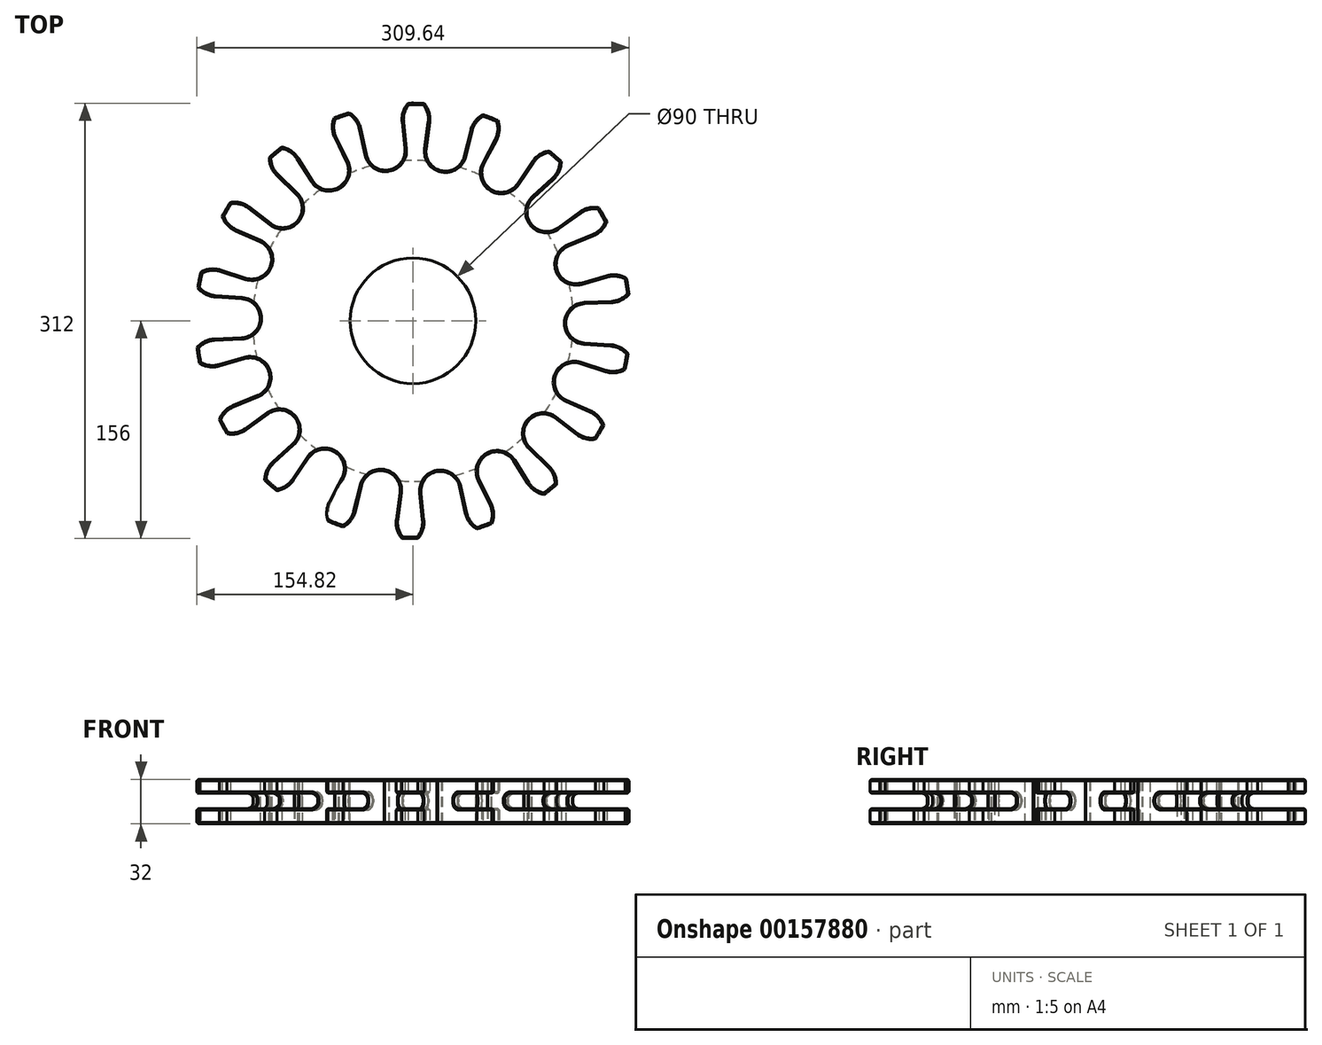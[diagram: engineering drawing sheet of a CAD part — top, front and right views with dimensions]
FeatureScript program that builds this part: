
annotation { "Feature Type Name" : "Feature", "Feature Type Description" : "" }
export const myFeature = defineFeature(function(context is Context, id is Id, definition is map)
    precondition{}
    {
        {
            var Q0;
            Q0=qCreatedBy(makeId("Top.planeOp"),FACE);
            var sketch = newSketch(context, id + "F0", { "sketchPlane" : qUnion([Q0])});
            skCircle(sketch, "E0", {"center": v(0, 0) * mm, "radius": 158.3 * mm, "construction": true});
            skArc(sketch, "E1", {"start": v(-102.28, 39.14) * mm, "mid": v(-102.55, 49.4) * mm, "end": v(-109.74, 56.72) * mm});
            skLineSegment(sketch, "E2", {"start": v(-109.74, 56.72) * mm, "end": v(-127.33, 64.55) * mm});
            skArc(sketch, "E3", {"start": v(-127.33, 64.55) * mm, "mid": v(-133.16, 68.77) * mm, "end": v(-136.8, 74.97) * mm});
            skArc(sketch, "E4", {"start": v(-136.8, 74.97) * mm, "mid": v(-133.95, 79.96) * mm, "end": v(-130.91, 84.84) * mm});
            skArc(sketch, "E5", {"start": v(-130.91, 84.84) * mm, "mid": v(-123.72, 84.58) * mm, "end": v(-117.25, 81.44) * mm});
            skLineSegment(sketch, "E6", {"start": v(-117.25, 81.44) * mm, "end": v(-102, 69.68) * mm});
            skArc(sketch, "E7", {"start": v(-102, 69.68) * mm, "mid": v(-92.15, 66.82) * mm, "end": v(-83, 71.46) * mm});
            skLineSegment(sketch, "E8", {"start": v(-83, 71.46) * mm, "end": v(-82.72, 71.76) * mm});
            skArc(sketch, "E9", {"start": v(-82.72, 71.76) * mm, "mid": v(-79.47, 81.5) * mm, "end": v(-83.72, 90.83) * mm});
            skLineSegment(sketch, "E10", {"start": v(-83.72, 90.83) * mm, "end": v(-97.57, 104.2) * mm});
            skArc(sketch, "E11", {"start": v(-97.57, 104.2) * mm, "mid": v(-101.6, 110.16) * mm, "end": v(-102.91, 117.24) * mm});
            skArc(sketch, "E12", {"start": v(-102.91, 117.24) * mm, "mid": v(-98.52, 120.95) * mm, "end": v(-94, 124.5) * mm});
            skArc(sketch, "E13", {"start": v(-94, 124.5) * mm, "mid": v(-87.33, 121.8) * mm, "end": v(-82.32, 116.63) * mm});
            skLineSegment(sketch, "E14", {"start": v(-82.32, 116.63) * mm, "end": v(-72.02, 100.36) * mm});
            skArc(sketch, "E15", {"start": v(-72.02, 100.36) * mm, "mid": v(-63.74, 94.31) * mm, "end": v(-53.55, 95.53) * mm});
            skLineSegment(sketch, "E16", {"start": v(-53.55, 95.53) * mm, "end": v(-53.2, 95.73) * mm});
            skArc(sketch, "E17", {"start": v(-53.2, 95.73) * mm, "mid": v(-46.8, 103.76) * mm, "end": v(-47.6, 113.99) * mm});
            skLineSegment(sketch, "E18", {"start": v(-47.6, 113.99) * mm, "end": v(-56.04, 131.3) * mm});
            skArc(sketch, "E19", {"start": v(-56.04, 131.3) * mm, "mid": v(-57.8, 138.27) * mm, "end": v(-56.6, 145.37) * mm});
            skArc(sketch, "E20", {"start": v(-56.6, 145.37) * mm, "mid": v(-51.21, 147.35) * mm, "end": v(-45.75, 149.14) * mm});
            skArc(sketch, "E21", {"start": v(-45.75, 149.14) * mm, "mid": v(-40.41, 144.32) * mm, "end": v(-37.46, 137.75) * mm});
            skLineSegment(sketch, "E22", {"start": v(-37.46, 137.75) * mm, "end": v(-33.35, 118.94) * mm});
            skArc(sketch, "E23", {"start": v(-33.35, 118.94) * mm, "mid": v(-27.64, 110.42) * mm, "end": v(-17.64, 108.08) * mm});
            skLineSegment(sketch, "E24", {"start": v(-17.64, 108.08) * mm, "end": v(-17.24, 108.15) * mm});
            skArc(sketch, "E25", {"start": v(-17.24, 108.15) * mm, "mid": v(-8.5, 113.5) * mm, "end": v(-5.75, 123.4) * mm});
            skLineSegment(sketch, "E26", {"start": v(-5.75, 123.4) * mm, "end": v(-7.76, 142.55) * mm});
            skArc(sketch, "E27", {"start": v(-7.76, 142.55) * mm, "mid": v(-7.02, 149.7) * mm, "end": v(-3.48, 155.96) * mm});
            skArc(sketch, "E28", {"start": v(-3.48, 155.96) * mm, "mid": v(2.27, 155.98) * mm, "end": v(8.02, 155.8) * mm});
            skArc(sketch, "E29", {"start": v(8.02, 155.8) * mm, "mid": v(11.38, 149.43) * mm, "end": v(11.9, 142.26) * mm});
            skLineSegment(sketch, "E30", {"start": v(11.9, 142.26) * mm, "end": v(9.34, 123.18) * mm});
            skArc(sketch, "E31", {"start": v(9.34, 123.18) * mm, "mid": v(11.8, 113.21) * mm, "end": v(20.39, 107.6) * mm});
            skLineSegment(sketch, "E32", {"start": v(20.39, 107.6) * mm, "end": v(20.79, 107.52) * mm});
            skArc(sketch, "E33", {"start": v(20.79, 107.52) * mm, "mid": v(30.84, 109.57) * mm, "end": v(36.8, 117.92) * mm});
            skLineSegment(sketch, "E34", {"start": v(36.8, 117.92) * mm, "end": v(41.46, 136.6) * mm});
            skArc(sketch, "E35", {"start": v(41.46, 136.6) * mm, "mid": v(44.6, 143.08) * mm, "end": v(50.07, 147.74) * mm});
            skArc(sketch, "E36", {"start": v(50.07, 147.74) * mm, "mid": v(55.49, 145.8) * mm, "end": v(60.82, 143.65) * mm});
            skArc(sketch, "E37", {"start": v(60.82, 143.65) * mm, "mid": v(61.8, 136.53) * mm, "end": v(59.85, 129.6) * mm});
            skLineSegment(sketch, "E38", {"start": v(59.85, 129.6) * mm, "end": v(50.9, 112.55) * mm});
            skArc(sketch, "E39", {"start": v(50.9, 112.55) * mm, "mid": v(49.8, 102.35) * mm, "end": v(55.96, 94.14) * mm});
            skLineSegment(sketch, "E40", {"start": v(55.96, 94.14) * mm, "end": v(56.3, 93.93) * mm});
            skArc(sketch, "E41", {"start": v(56.3, 93.93) * mm, "mid": v(66.46, 92.41) * mm, "end": v(74.91, 98.22) * mm});
            skLineSegment(sketch, "E42", {"start": v(74.91, 98.22) * mm, "end": v(85.68, 114.18) * mm});
            skArc(sketch, "E43", {"start": v(85.68, 114.18) * mm, "mid": v(90.85, 119.2) * mm, "end": v(97.59, 121.7) * mm});
            skArc(sketch, "E44", {"start": v(97.59, 121.7) * mm, "mid": v(102, 118.03) * mm, "end": v(106.29, 114.19) * mm});
            skArc(sketch, "E45", {"start": v(106.29, 114.19) * mm, "mid": v(104.77, 107.16) * mm, "end": v(100.56, 101.32) * mm});
            skLineSegment(sketch, "E46", {"start": v(100.56, 101.32) * mm, "end": v(86.33, 88.35) * mm});
            skArc(sketch, "E47", {"start": v(86.33, 88.35) * mm, "mid": v(81.8, 79.14) * mm, "end": v(84.78, 69.32) * mm});
            skLineSegment(sketch, "E48", {"start": v(84.78, 69.32) * mm, "end": v(85.04, 69) * mm});
            skArc(sketch, "E49", {"start": v(85.04, 69) * mm, "mid": v(94.06, 64.1) * mm, "end": v(104, 66.68) * mm});
            skLineSegment(sketch, "E50", {"start": v(104, 66.68) * mm, "end": v(119.57, 78) * mm});
            skArc(sketch, "E51", {"start": v(119.57, 78) * mm, "mid": v(126.13, 80.93) * mm, "end": v(133.33, 81) * mm});
            skArc(sketch, "E52", {"start": v(133.33, 81) * mm, "mid": v(136.22, 76.02) * mm, "end": v(138.93, 70.95) * mm});
            skArc(sketch, "E53", {"start": v(138.93, 70.95) * mm, "mid": v(135.1, 64.86) * mm, "end": v(129.15, 60.82) * mm});
            skLineSegment(sketch, "E54", {"start": v(129.15, 60.82) * mm, "end": v(111.35, 53.5) * mm});
            skArc(sketch, "E55", {"start": v(111.35, 53.5) * mm, "mid": v(103.94, 46.4) * mm, "end": v(103.38, 36.15) * mm});
            skLineSegment(sketch, "E56", {"start": v(103.38, 36.15) * mm, "end": v(103.51, 35.76) * mm});
            skArc(sketch, "E57", {"start": v(103.51, 35.76) * mm, "mid": v(110.31, 28.07) * mm, "end": v(120.52, 27.09) * mm});
            skLineSegment(sketch, "E58", {"start": v(120.52, 27.09) * mm, "end": v(139.03, 32.4) * mm});
            skArc(sketch, "E59", {"start": v(139.03, 32.4) * mm, "mid": v(146.2, 32.91) * mm, "end": v(152.99, 30.5) * mm});
            skArc(sketch, "E60", {"start": v(152.99, 30.5) * mm, "mid": v(154, 24.85) * mm, "end": v(154.82, 19.15) * mm});
            skArc(sketch, "E61", {"start": v(154.82, 19.15) * mm, "mid": v(149.14, 14.74) * mm, "end": v(142.17, 12.98) * mm});
            skLineSegment(sketch, "E62", {"start": v(142.17, 12.98) * mm, "end": v(122.93, 12.19) * mm});
            skArc(sketch, "E63", {"start": v(122.93, 12.19) * mm, "mid": v(113.54, 8.04) * mm, "end": v(109.5, -1.4) * mm});
            skLineSegment(sketch, "E64", {"start": v(109.5, -1.4) * mm, "end": v(109.5, -1.8) * mm});
            skArc(sketch, "E65", {"start": v(109.5, -1.8) * mm, "mid": v(113.26, -11.35) * mm, "end": v(122.52, -15.77) * mm});
            skLineSegment(sketch, "E66", {"start": v(122.52, -15.77) * mm, "end": v(141.73, -17.11) * mm});
            skArc(sketch, "E67", {"start": v(141.73, -17.11) * mm, "mid": v(148.65, -19.08) * mm, "end": v(154.2, -23.66) * mm});
            skArc(sketch, "E68", {"start": v(154.2, -23.66) * mm, "mid": v(153.22, -29.33) * mm, "end": v(152.03, -34.95) * mm});
            skArc(sketch, "E69", {"start": v(152.03, -34.95) * mm, "mid": v(145.19, -37.16) * mm, "end": v(138.03, -36.43) * mm});
            skLineSegment(sketch, "E70", {"start": v(138.03, -36.43) * mm, "end": v(119.68, -30.6) * mm});
            skArc(sketch, "E71", {"start": v(119.68, -30.6) * mm, "mid": v(109.45, -31.28) * mm, "end": v(102.43, -38.76) * mm});
            skLineSegment(sketch, "E72", {"start": v(102.43, -38.76) * mm, "end": v(102.28, -39.14) * mm});
            skArc(sketch, "E73", {"start": v(102.28, -39.14) * mm, "mid": v(102.55, -49.4) * mm, "end": v(109.74, -56.72) * mm});
            skLineSegment(sketch, "E74", {"start": v(109.74, -56.72) * mm, "end": v(127.33, -64.55) * mm});
            skArc(sketch, "E75", {"start": v(127.33, -64.55) * mm, "mid": v(133.16, -68.77) * mm, "end": v(136.8, -74.97) * mm});
            skArc(sketch, "E76", {"start": v(136.8, -74.97) * mm, "mid": v(133.95, -79.96) * mm, "end": v(130.91, -84.84) * mm});
            skArc(sketch, "E77", {"start": v(130.91, -84.84) * mm, "mid": v(123.72, -84.58) * mm, "end": v(117.25, -81.44) * mm});
            skLineSegment(sketch, "E78", {"start": v(117.25, -81.44) * mm, "end": v(102, -69.68) * mm});
            skArc(sketch, "E79", {"start": v(102, -69.68) * mm, "mid": v(92.15, -66.82) * mm, "end": v(83, -71.46) * mm});
            skLineSegment(sketch, "E80", {"start": v(83, -71.46) * mm, "end": v(82.72, -71.76) * mm});
            skArc(sketch, "E81", {"start": v(82.72, -71.76) * mm, "mid": v(79.47, -81.5) * mm, "end": v(83.72, -90.83) * mm});
            skLineSegment(sketch, "E82", {"start": v(83.72, -90.83) * mm, "end": v(97.57, -104.2) * mm});
            skArc(sketch, "E83", {"start": v(97.57, -104.2) * mm, "mid": v(101.6, -110.16) * mm, "end": v(102.91, -117.24) * mm});
            skArc(sketch, "E84", {"start": v(102.91, -117.24) * mm, "mid": v(98.52, -120.95) * mm, "end": v(94, -124.5) * mm});
            skArc(sketch, "E85", {"start": v(94, -124.5) * mm, "mid": v(87.33, -121.8) * mm, "end": v(82.32, -116.63) * mm});
            skLineSegment(sketch, "E86", {"start": v(82.32, -116.63) * mm, "end": v(72.02, -100.36) * mm});
            skArc(sketch, "E87", {"start": v(72.02, -100.36) * mm, "mid": v(63.74, -94.31) * mm, "end": v(53.55, -95.53) * mm});
            skLineSegment(sketch, "E88", {"start": v(53.55, -95.53) * mm, "end": v(53.2, -95.73) * mm});
            skArc(sketch, "E89", {"start": v(53.2, -95.73) * mm, "mid": v(46.8, -103.76) * mm, "end": v(47.6, -113.99) * mm});
            skLineSegment(sketch, "E90", {"start": v(47.6, -113.99) * mm, "end": v(56.04, -131.3) * mm});
            skArc(sketch, "E91", {"start": v(56.04, -131.3) * mm, "mid": v(57.8, -138.27) * mm, "end": v(56.6, -145.37) * mm});
            skArc(sketch, "E92", {"start": v(56.6, -145.37) * mm, "mid": v(51.21, -147.35) * mm, "end": v(45.75, -149.14) * mm});
            skArc(sketch, "E93", {"start": v(45.75, -149.14) * mm, "mid": v(40.41, -144.32) * mm, "end": v(37.46, -137.75) * mm});
            skLineSegment(sketch, "E94", {"start": v(37.46, -137.75) * mm, "end": v(33.35, -118.94) * mm});
            skArc(sketch, "E95", {"start": v(33.35, -118.94) * mm, "mid": v(27.64, -110.42) * mm, "end": v(17.64, -108.08) * mm});
            skLineSegment(sketch, "E96", {"start": v(17.64, -108.08) * mm, "end": v(17.24, -108.15) * mm});
            skArc(sketch, "E97", {"start": v(17.24, -108.15) * mm, "mid": v(8.5, -113.5) * mm, "end": v(5.75, -123.4) * mm});
            skLineSegment(sketch, "E98", {"start": v(5.75, -123.4) * mm, "end": v(7.76, -142.55) * mm});
            skArc(sketch, "E99", {"start": v(7.76, -142.55) * mm, "mid": v(7.02, -149.7) * mm, "end": v(3.48, -155.96) * mm});
            skArc(sketch, "E100", {"start": v(3.48, -155.96) * mm, "mid": v(-2.27, -155.98) * mm, "end": v(-8.02, -155.8) * mm});
            skArc(sketch, "E101", {"start": v(-8.02, -155.8) * mm, "mid": v(-11.38, -149.43) * mm, "end": v(-11.9, -142.26) * mm});
            skLineSegment(sketch, "E102", {"start": v(-11.9, -142.26) * mm, "end": v(-9.34, -123.18) * mm});
            skArc(sketch, "E103", {"start": v(-9.34, -123.18) * mm, "mid": v(-11.8, -113.21) * mm, "end": v(-20.39, -107.6) * mm});
            skLineSegment(sketch, "E104", {"start": v(-20.39, -107.6) * mm, "end": v(-20.79, -107.52) * mm});
            skArc(sketch, "E105", {"start": v(-20.79, -107.52) * mm, "mid": v(-30.84, -109.57) * mm, "end": v(-36.8, -117.92) * mm});
            skLineSegment(sketch, "E106", {"start": v(-36.8, -117.92) * mm, "end": v(-41.46, -136.6) * mm});
            skArc(sketch, "E107", {"start": v(-41.46, -136.6) * mm, "mid": v(-44.6, -143.08) * mm, "end": v(-50.07, -147.74) * mm});
            skArc(sketch, "E108", {"start": v(-50.07, -147.74) * mm, "mid": v(-55.49, -145.8) * mm, "end": v(-60.82, -143.65) * mm});
            skArc(sketch, "E109", {"start": v(-60.82, -143.65) * mm, "mid": v(-61.8, -136.53) * mm, "end": v(-59.85, -129.6) * mm});
            skLineSegment(sketch, "E110", {"start": v(-59.85, -129.6) * mm, "end": v(-50.9, -112.55) * mm});
            skArc(sketch, "E111", {"start": v(-50.9, -112.55) * mm, "mid": v(-49.8, -102.35) * mm, "end": v(-55.96, -94.14) * mm});
            skLineSegment(sketch, "E112", {"start": v(-55.96, -94.14) * mm, "end": v(-56.3, -93.93) * mm});
            skArc(sketch, "E113", {"start": v(-56.3, -93.93) * mm, "mid": v(-66.46, -92.41) * mm, "end": v(-74.91, -98.22) * mm});
            skLineSegment(sketch, "E114", {"start": v(-74.91, -98.22) * mm, "end": v(-85.68, -114.18) * mm});
            skArc(sketch, "E115", {"start": v(-85.68, -114.18) * mm, "mid": v(-90.85, -119.2) * mm, "end": v(-97.59, -121.7) * mm});
            skArc(sketch, "E116", {"start": v(-97.59, -121.7) * mm, "mid": v(-102, -118.03) * mm, "end": v(-106.29, -114.19) * mm});
            skArc(sketch, "E117", {"start": v(-106.29, -114.19) * mm, "mid": v(-104.77, -107.16) * mm, "end": v(-100.56, -101.32) * mm});
            skLineSegment(sketch, "E118", {"start": v(-100.56, -101.32) * mm, "end": v(-86.33, -88.35) * mm});
            skArc(sketch, "E119", {"start": v(-86.33, -88.35) * mm, "mid": v(-81.8, -79.14) * mm, "end": v(-84.78, -69.32) * mm});
            skLineSegment(sketch, "E120", {"start": v(-84.78, -69.32) * mm, "end": v(-85.04, -69) * mm});
            skArc(sketch, "E121", {"start": v(-85.04, -69) * mm, "mid": v(-94.06, -64.1) * mm, "end": v(-104, -66.68) * mm});
            skLineSegment(sketch, "E122", {"start": v(-104, -66.68) * mm, "end": v(-119.57, -78) * mm});
            skArc(sketch, "E123", {"start": v(-119.57, -78) * mm, "mid": v(-126.13, -80.93) * mm, "end": v(-133.33, -81) * mm});
            skArc(sketch, "E124", {"start": v(-133.33, -81) * mm, "mid": v(-136.22, -76.02) * mm, "end": v(-138.93, -70.95) * mm});
            skArc(sketch, "E125", {"start": v(-138.93, -70.95) * mm, "mid": v(-135.1, -64.86) * mm, "end": v(-129.15, -60.82) * mm});
            skLineSegment(sketch, "E126", {"start": v(-129.15, -60.82) * mm, "end": v(-111.35, -53.5) * mm});
            skArc(sketch, "E127", {"start": v(-111.35, -53.5) * mm, "mid": v(-103.94, -46.4) * mm, "end": v(-103.38, -36.15) * mm});
            skLineSegment(sketch, "E128", {"start": v(-103.38, -36.15) * mm, "end": v(-103.51, -35.76) * mm});
            skArc(sketch, "E129", {"start": v(-103.51, -35.76) * mm, "mid": v(-110.31, -28.07) * mm, "end": v(-120.52, -27.09) * mm});
            skLineSegment(sketch, "E130", {"start": v(-120.52, -27.09) * mm, "end": v(-139.03, -32.4) * mm});
            skArc(sketch, "E131", {"start": v(-139.03, -32.4) * mm, "mid": v(-146.2, -32.91) * mm, "end": v(-152.99, -30.5) * mm});
            skArc(sketch, "E132", {"start": v(-152.99, -30.5) * mm, "mid": v(-154, -24.85) * mm, "end": v(-154.82, -19.15) * mm});
            skArc(sketch, "E133", {"start": v(-154.82, -19.15) * mm, "mid": v(-149.14, -14.74) * mm, "end": v(-142.17, -12.98) * mm});
            skLineSegment(sketch, "E134", {"start": v(-142.17, -12.98) * mm, "end": v(-122.93, -12.19) * mm});
            skArc(sketch, "E135", {"start": v(-122.93, -12.19) * mm, "mid": v(-113.54, -8.04) * mm, "end": v(-109.5, 1.4) * mm});
            skLineSegment(sketch, "E136", {"start": v(-109.5, 1.4) * mm, "end": v(-109.5, 1.8) * mm});
            skArc(sketch, "E137", {"start": v(-109.5, 1.8) * mm, "mid": v(-113.26, 11.35) * mm, "end": v(-122.52, 15.77) * mm});
            skLineSegment(sketch, "E138", {"start": v(-122.52, 15.77) * mm, "end": v(-141.73, 17.11) * mm});
            skArc(sketch, "E139", {"start": v(-141.73, 17.11) * mm, "mid": v(-148.65, 19.08) * mm, "end": v(-154.2, 23.66) * mm});
            skArc(sketch, "E140", {"start": v(-154.2, 23.66) * mm, "mid": v(-153.22, 29.33) * mm, "end": v(-152.03, 34.95) * mm});
            skArc(sketch, "E141", {"start": v(-152.03, 34.95) * mm, "mid": v(-145.19, 37.16) * mm, "end": v(-138.03, 36.43) * mm});
            skLineSegment(sketch, "E142", {"start": v(-138.03, 36.43) * mm, "end": v(-119.68, 30.6) * mm});
            skArc(sketch, "E143", {"start": v(-119.68, 30.6) * mm, "mid": v(-109.45, 31.28) * mm, "end": v(-102.43, 38.76) * mm});
            skLineSegment(sketch, "E144", {"start": v(-102.43, 38.76) * mm, "end": v(-102.28, 39.14) * mm});
            skCircle(sketch, "E145", {"center": v(0, 0) * mm, "radius": 74.9 * mm, "construction": true});
            skSolve(sketch);
        }
        {
            var Q0;
            Q0=qSketchRegion(id+"F0",true);
            extrude(context, id + "F1", {"entities" : qUnion([Q0]), "endBound" : BoundingType.SYMMETRIC, "depth" : 32 * mm});
        }
        {
            var Q0;
            Q0=qCreatedBy(makeId("Top.planeOp"),FACE);
            var sketch = newSketch(context, id + "F2", { "sketchPlane" : qUnion([Q0])});
            skCircle(sketch, "E146", {"center": v(0, 0) * mm, "radius": 45 * mm});
            skSolve(sketch);
        }
        {
            var Q0;
            Q0=qSketchRegion(id+"F2",true);
            extrude(context, id + "F3", {"entities" : qUnion([Q0]), "operationType" : NewBodyOperationType.REMOVE, "endBound" : BoundingType.SYMMETRIC, "oppositeDirection" : true, "depth" : 91.5 * mm});
        }
        {
            var Q0;
            Q0=qCreatedBy(makeId("Right.planeOp"),FACE);
            var sketch = newSketch(context, id + "F4", { "sketchPlane" : qUnion([Q0])});
            skLineSegment(sketch, "E147.bottom", {"start": v(-163.5, 6) * mm, "end": v(-119.5, 6) * mm});
            skLineSegment(sketch, "E147.top", {"start": v(-163.5, -5) * mm, "end": v(-119.5, -5) * mm});
            skLineSegment(sketch, "E147.left", {"start": v(-163.5, 6) * mm, "end": v(-163.5, -5) * mm});
            skLineSegment(sketch, "E147.right", {"start": v(-115, 1.5) * mm, "end": v(-115, -0.5) * mm});
            skPoint(sketch, "E148.visualSharp", {"position": v(-115, 6) * mm});
            skArc(sketch, "E148.filletArc", {"start": v(-115, 1.5) * mm, "mid": v(-116.32, 4.68) * mm, "end": v(-119.5, 6) * mm});
            skPoint(sketch, "E149.visualSharp", {"position": v(-115, -5) * mm});
            skArc(sketch, "E149.filletArc", {"start": v(-119.5, -5) * mm, "mid": v(-116.32, -3.68) * mm, "end": v(-115, -0.5) * mm});
            skSolve(sketch);
        }
        {
            var Q0;
            Q0=qSketchRegion(id+"F4",true);
            var Q1;
            Q1=makeQuery(id+"F3.boolean.opBoolean","COPY",FACE,{"derivedFrom":makeQuery(id+"F3.opExtrude","SWEPT_FACE",FACE,{"disambiguationData":[OSD([sQuery(id+"F2.wireOp",EDGE,"E146")])]})});
            revolve(context, id + "F5", {"operationType" : NewBodyOperationType.REMOVE, "entities" : qUnion([Q0]), "axis" : qUnion([Q1]), "revolveType" : RevolveType.FULL, "oppositeDirection" : true});
        }
        {
            var Q0;
            Q0=makeQuery(id+"F1.opExtrude","CAP_EDGE",EDGE,{"disambiguationData":[OSD([sQuery(id+"F0.wireOp",EDGE,"E113")])],"isStart":false});
            var Q1;
            Q1=makeQuery(id+"F1.opExtrude","CAP_EDGE",EDGE,{"disambiguationData":[OSD([sQuery(id+"F0.wireOp",EDGE,"E121")])],"isStart":false});
            var Q2;
            Q2=makeQuery(id+"F1.opExtrude","CAP_EDGE",EDGE,{"disambiguationData":[OSD([sQuery(id+"F0.wireOp",EDGE,"E129")])],"isStart":false});
            var Q3;
            Q3=makeQuery(id+"F1.opExtrude","CAP_EDGE",EDGE,{"disambiguationData":[OSD([sQuery(id+"F0.wireOp",EDGE,"E137")])],"isStart":false});
            var Q4;
            Q4=makeQuery(id+"F1.opExtrude","CAP_EDGE",EDGE,{"disambiguationData":[OSD([sQuery(id+"F0.wireOp",EDGE,"E1")])],"isStart":false});
            var Q5;
            Q5=makeQuery(id+"F1.opExtrude","CAP_EDGE",EDGE,{"disambiguationData":[OSD([sQuery(id+"F0.wireOp",EDGE,"E9")])],"isStart":false});
            var Q6;
            Q6=makeQuery(id+"F1.opExtrude","CAP_EDGE",EDGE,{"disambiguationData":[OSD([sQuery(id+"F0.wireOp",EDGE,"E17")])],"isStart":false});
            var Q7;
            Q7=makeQuery(id+"F1.opExtrude","CAP_EDGE",EDGE,{"disambiguationData":[OSD([sQuery(id+"F0.wireOp",EDGE,"E25")])],"isStart":false});
            var Q8;
            Q8=makeQuery(id+"F1.opExtrude","CAP_EDGE",EDGE,{"disambiguationData":[OSD([sQuery(id+"F0.wireOp",EDGE,"E33")])],"isStart":false});
            var Q9;
            Q9=makeQuery(id+"F1.opExtrude","CAP_EDGE",EDGE,{"disambiguationData":[OSD([sQuery(id+"F0.wireOp",EDGE,"E41")])],"isStart":false});
            var Q10;
            Q10=makeQuery(id+"F1.opExtrude","CAP_EDGE",EDGE,{"disambiguationData":[OSD([sQuery(id+"F0.wireOp",EDGE,"E50")])],"isStart":false});
            var Q11;
            Q11=makeQuery(id+"F1.opExtrude","CAP_EDGE",EDGE,{"disambiguationData":[OSD([sQuery(id+"F0.wireOp",EDGE,"E58")])],"isStart":false});
            var Q12;
            Q12=makeQuery(id+"F1.opExtrude","CAP_EDGE",EDGE,{"disambiguationData":[OSD([sQuery(id+"F0.wireOp",EDGE,"E65")])],"isStart":false});
            var Q13;
            Q13=makeQuery(id+"F1.opExtrude","CAP_EDGE",EDGE,{"disambiguationData":[OSD([sQuery(id+"F0.wireOp",EDGE,"E73")])],"isStart":false});
            var Q14;
            Q14=makeQuery(id+"F1.opExtrude","CAP_EDGE",EDGE,{"disambiguationData":[OSD([sQuery(id+"F0.wireOp",EDGE,"E81")])],"isStart":false});
            var Q15;
            Q15=makeQuery(id+"F1.opExtrude","CAP_EDGE",EDGE,{"disambiguationData":[OSD([sQuery(id+"F0.wireOp",EDGE,"E89")])],"isStart":false});
            var Q16;
            Q16=makeQuery(id+"F1.opExtrude","CAP_EDGE",EDGE,{"disambiguationData":[OSD([sQuery(id+"F0.wireOp",EDGE,"E97")])],"isStart":false});
            var Q17;
            Q17=makeQuery(id+"F1.opExtrude","CAP_EDGE",EDGE,{"disambiguationData":[OSD([sQuery(id+"F0.wireOp",EDGE,"E105")])],"isStart":false});
            var Q18;
            Q18=makeQuery(id+"F1.opExtrude","CAP_EDGE",EDGE,{"disambiguationData":[OSD([sQuery(id+"F0.wireOp",EDGE,"E103")])],"isStart":false});
            var Q19;
            Q19=makeQuery(id+"F1.opExtrude","CAP_EDGE",EDGE,{"disambiguationData":[OSD([sQuery(id+"F0.wireOp",EDGE,"E95")])],"isStart":false});
            var Q20;
            Q20=makeQuery(id+"F1.opExtrude","CAP_EDGE",EDGE,{"disambiguationData":[OSD([sQuery(id+"F0.wireOp",EDGE,"E87")])],"isStart":false});
            var Q21;
            Q21=makeQuery(id+"F1.opExtrude","CAP_EDGE",EDGE,{"disambiguationData":[OSD([sQuery(id+"F0.wireOp",EDGE,"E79")])],"isStart":false});
            var Q22;
            Q22=makeQuery(id+"F1.opExtrude","CAP_EDGE",EDGE,{"disambiguationData":[OSD([sQuery(id+"F0.wireOp",EDGE,"E71")])],"isStart":false});
            var Q23;
            Q23=makeQuery(id+"F1.opExtrude","CAP_EDGE",EDGE,{"disambiguationData":[OSD([sQuery(id+"F0.wireOp",EDGE,"E63")])],"isStart":false});
            var Q24;
            Q24=makeQuery(id+"F1.opExtrude","CAP_EDGE",EDGE,{"disambiguationData":[OSD([sQuery(id+"F0.wireOp",EDGE,"E55")])],"isStart":false});
            var Q25;
            Q25=makeQuery(id+"F1.opExtrude","CAP_EDGE",EDGE,{"disambiguationData":[OSD([sQuery(id+"F0.wireOp",EDGE,"E47")])],"isStart":false});
            var Q26;
            Q26=makeQuery(id+"F1.opExtrude","CAP_EDGE",EDGE,{"disambiguationData":[OSD([sQuery(id+"F0.wireOp",EDGE,"E119")])],"isStart":false});
            var Q27;
            Q27=makeQuery(id+"F1.opExtrude","CAP_EDGE",EDGE,{"disambiguationData":[OSD([sQuery(id+"F0.wireOp",EDGE,"E127")])],"isStart":false});
            var Q28;
            Q28=makeQuery(id+"F1.opExtrude","CAP_EDGE",EDGE,{"disambiguationData":[OSD([sQuery(id+"F0.wireOp",EDGE,"E135")])],"isStart":false});
            var Q29;
            Q29=makeQuery(id+"F1.opExtrude","CAP_EDGE",EDGE,{"disambiguationData":[OSD([sQuery(id+"F0.wireOp",EDGE,"E143")])],"isStart":false});
            var Q30;
            Q30=makeQuery(id+"F1.opExtrude","CAP_EDGE",EDGE,{"disambiguationData":[OSD([sQuery(id+"F0.wireOp",EDGE,"E7")])],"isStart":false});
            var Q31;
            Q31=makeQuery(id+"F1.opExtrude","CAP_EDGE",EDGE,{"disambiguationData":[OSD([sQuery(id+"F0.wireOp",EDGE,"E15")])],"isStart":false});
            var Q32;
            Q32=makeQuery(id+"F1.opExtrude","CAP_EDGE",EDGE,{"disambiguationData":[OSD([sQuery(id+"F0.wireOp",EDGE,"E23")])],"isStart":false});
            var Q33;
            Q33=makeQuery(id+"F1.opExtrude","CAP_EDGE",EDGE,{"disambiguationData":[OSD([sQuery(id+"F0.wireOp",EDGE,"E31")])],"isStart":false});
            var Q34;
            Q34=makeQuery(id+"F1.opExtrude","CAP_EDGE",EDGE,{"disambiguationData":[OSD([sQuery(id+"F0.wireOp",EDGE,"E39")])],"isStart":false});
            var Q35;
            Q35=makeQuery(id+"F1.opExtrude","CAP_EDGE",EDGE,{"disambiguationData":[OSD([sQuery(id+"F0.wireOp",EDGE,"E100")])],"isStart":false});
            var Q36;
            Q36=makeQuery(id+"F1.opExtrude","CAP_EDGE",EDGE,{"disambiguationData":[OSD([sQuery(id+"F0.wireOp",EDGE,"E108")])],"isStart":false});
            var Q37;
            Q37=makeQuery(id+"F1.opExtrude","CAP_EDGE",EDGE,{"disambiguationData":[OSD([sQuery(id+"F0.wireOp",EDGE,"E116")])],"isStart":false});
            var Q38;
            Q38=makeQuery(id+"F1.opExtrude","CAP_EDGE",EDGE,{"disambiguationData":[OSD([sQuery(id+"F0.wireOp",EDGE,"E124")])],"isStart":false});
            var Q39;
            Q39=makeQuery(id+"F1.opExtrude","CAP_EDGE",EDGE,{"disambiguationData":[OSD([sQuery(id+"F0.wireOp",EDGE,"E132")])],"isStart":false});
            var Q40;
            Q40=makeQuery(id+"F1.opExtrude","CAP_EDGE",EDGE,{"disambiguationData":[OSD([sQuery(id+"F0.wireOp",EDGE,"E140")])],"isStart":false});
            var Q41;
            Q41=makeQuery(id+"F1.opExtrude","CAP_EDGE",EDGE,{"disambiguationData":[OSD([sQuery(id+"F0.wireOp",EDGE,"E4")])],"isStart":false});
            var Q42;
            Q42=makeQuery(id+"F1.opExtrude","CAP_EDGE",EDGE,{"disambiguationData":[OSD([sQuery(id+"F0.wireOp",EDGE,"E12")])],"isStart":false});
            var Q43;
            Q43=makeQuery(id+"F1.opExtrude","CAP_EDGE",EDGE,{"disambiguationData":[OSD([sQuery(id+"F0.wireOp",EDGE,"E20")])],"isStart":false});
            var Q44;
            Q44=makeQuery(id+"F1.opExtrude","CAP_EDGE",EDGE,{"disambiguationData":[OSD([sQuery(id+"F0.wireOp",EDGE,"E28")])],"isStart":false});
            var Q45;
            Q45=makeQuery(id+"F1.opExtrude","CAP_EDGE",EDGE,{"disambiguationData":[OSD([sQuery(id+"F0.wireOp",EDGE,"E36")])],"isStart":false});
            var Q46;
            Q46=makeQuery(id+"F1.opExtrude","CAP_EDGE",EDGE,{"disambiguationData":[OSD([sQuery(id+"F0.wireOp",EDGE,"E44")])],"isStart":false});
            var Q47;
            Q47=makeQuery(id+"F1.opExtrude","CAP_EDGE",EDGE,{"disambiguationData":[OSD([sQuery(id+"F0.wireOp",EDGE,"E52")])],"isStart":false});
            var Q48;
            Q48=makeQuery(id+"F1.opExtrude","CAP_EDGE",EDGE,{"disambiguationData":[OSD([sQuery(id+"F0.wireOp",EDGE,"E60")])],"isStart":false});
            var Q49;
            Q49=makeQuery(id+"F1.opExtrude","CAP_EDGE",EDGE,{"disambiguationData":[OSD([sQuery(id+"F0.wireOp",EDGE,"E68")])],"isStart":false});
            var Q50;
            Q50=makeQuery(id+"F1.opExtrude","CAP_EDGE",EDGE,{"disambiguationData":[OSD([sQuery(id+"F0.wireOp",EDGE,"E76")])],"isStart":false});
            var Q51;
            Q51=makeQuery(id+"F1.opExtrude","CAP_EDGE",EDGE,{"disambiguationData":[OSD([sQuery(id+"F0.wireOp",EDGE,"E84")])],"isStart":false});
            var Q52;
            Q52=makeQuery(id+"F1.opExtrude","CAP_EDGE",EDGE,{"disambiguationData":[OSD([sQuery(id+"F0.wireOp",EDGE,"E92")])],"isStart":false});
            var Q53;
            Q53=makeQuery(id+"F5.boolean.opBoolean","INTERSECT",EDGE,{"derivedFrom":[makeQuery(id+"F1.opExtrude","SWEPT_FACE",FACE,{"disambiguationData":[OSD([sQuery(id+"F0.wireOp",EDGE,"E89")])]}),makeQuery(id+"F5.opRevolve","SWEPT_FACE",FACE,{"disambiguationData":[OSD([sQuery(id+"F4.wireOp",EDGE,"E149.filletArc")])]})]});
            var Q54;
            Q54=makeQuery(id+"F5.boolean.opBoolean","INTERSECT",EDGE,{"derivedFrom":[makeQuery(id+"F1.opExtrude","SWEPT_FACE",FACE,{"disambiguationData":[OSD([sQuery(id+"F0.wireOp",EDGE,"E81")])]}),makeQuery(id+"F5.opRevolve","SWEPT_FACE",FACE,{"disambiguationData":[OSD([sQuery(id+"F4.wireOp",EDGE,"E149.filletArc")])]})]});
            var Q55;
            Q55=makeQuery(id+"F5.boolean.opBoolean","INTERSECT",EDGE,{"derivedFrom":[makeQuery(id+"F1.opExtrude","SWEPT_FACE",FACE,{"disambiguationData":[OSD([sQuery(id+"F0.wireOp",EDGE,"E79")])]}),makeQuery(id+"F5.opRevolve","SWEPT_FACE",FACE,{"disambiguationData":[OSD([sQuery(id+"F4.wireOp",EDGE,"E149.filletArc")])]})]});
            var Q56;
            Q56=makeQuery(id+"F5.boolean.opBoolean","INTERSECT",EDGE,{"derivedFrom":[makeQuery(id+"F1.opExtrude","SWEPT_FACE",FACE,{"disambiguationData":[OSD([sQuery(id+"F0.wireOp",EDGE,"E87")])]}),makeQuery(id+"F5.opRevolve","SWEPT_FACE",FACE,{"disambiguationData":[OSD([sQuery(id+"F4.wireOp",EDGE,"E149.filletArc")])]})]});
            var Q57;
            Q57=makeQuery(id+"F5.boolean.opBoolean","INTERSECT",EDGE,{"derivedFrom":[makeQuery(id+"F1.opExtrude","SWEPT_FACE",FACE,{"disambiguationData":[OSD([sQuery(id+"F0.wireOp",EDGE,"E95")])]}),makeQuery(id+"F5.opRevolve","SWEPT_FACE",FACE,{"disambiguationData":[OSD([sQuery(id+"F4.wireOp",EDGE,"E149.filletArc")])]})]});
            var Q58;
            Q58=makeQuery(id+"F5.boolean.opBoolean","INTERSECT",EDGE,{"derivedFrom":[makeQuery(id+"F1.opExtrude","SWEPT_FACE",FACE,{"disambiguationData":[OSD([sQuery(id+"F0.wireOp",EDGE,"E97")])]}),makeQuery(id+"F5.opRevolve","SWEPT_FACE",FACE,{"disambiguationData":[OSD([sQuery(id+"F4.wireOp",EDGE,"E149.filletArc")])]})]});
            var Q59;
            Q59=makeQuery(id+"F5.boolean.opBoolean","INTERSECT",EDGE,{"derivedFrom":[makeQuery(id+"F1.opExtrude","SWEPT_FACE",FACE,{"disambiguationData":[OSD([sQuery(id+"F0.wireOp",EDGE,"E105")])]}),makeQuery(id+"F5.opRevolve","SWEPT_FACE",FACE,{"disambiguationData":[OSD([sQuery(id+"F4.wireOp",EDGE,"E149.filletArc")])]})]});
            var Q60;
            Q60=makeQuery(id+"F5.boolean.opBoolean","INTERSECT",EDGE,{"derivedFrom":[makeQuery(id+"F1.opExtrude","SWEPT_FACE",FACE,{"disambiguationData":[OSD([sQuery(id+"F0.wireOp",EDGE,"E103")])]}),makeQuery(id+"F5.opRevolve","SWEPT_FACE",FACE,{"disambiguationData":[OSD([sQuery(id+"F4.wireOp",EDGE,"E149.filletArc")])]})]});
            var Q61;
            Q61=makeQuery(id+"F5.boolean.opBoolean","INTERSECT",EDGE,{"derivedFrom":[makeQuery(id+"F1.opExtrude","SWEPT_FACE",FACE,{"disambiguationData":[OSD([sQuery(id+"F0.wireOp",EDGE,"E111")])]}),makeQuery(id+"F5.opRevolve","SWEPT_FACE",FACE,{"disambiguationData":[OSD([sQuery(id+"F4.wireOp",EDGE,"E149.filletArc")])]})]});
            var Q62;
            Q62=makeQuery(id+"F5.boolean.opBoolean","INTERSECT",EDGE,{"derivedFrom":[makeQuery(id+"F1.opExtrude","SWEPT_FACE",FACE,{"disambiguationData":[OSD([sQuery(id+"F0.wireOp",EDGE,"E119")])]}),makeQuery(id+"F5.opRevolve","SWEPT_FACE",FACE,{"disambiguationData":[OSD([sQuery(id+"F4.wireOp",EDGE,"E149.filletArc")])]})]});
            var Q63;
            Q63=makeQuery(id+"F5.boolean.opBoolean","INTERSECT",EDGE,{"derivedFrom":[makeQuery(id+"F1.opExtrude","SWEPT_FACE",FACE,{"disambiguationData":[OSD([sQuery(id+"F0.wireOp",EDGE,"E121")])]}),makeQuery(id+"F5.opRevolve","SWEPT_FACE",FACE,{"disambiguationData":[OSD([sQuery(id+"F4.wireOp",EDGE,"E149.filletArc")])]})]});
            var Q64;
            Q64=makeQuery(id+"F5.boolean.opBoolean","INTERSECT",EDGE,{"derivedFrom":[makeQuery(id+"F1.opExtrude","SWEPT_FACE",FACE,{"disambiguationData":[OSD([sQuery(id+"F0.wireOp",EDGE,"E113")])]}),makeQuery(id+"F5.opRevolve","SWEPT_FACE",FACE,{"disambiguationData":[OSD([sQuery(id+"F4.wireOp",EDGE,"E149.filletArc")])]})]});
            var Q65;
            Q65=makeQuery(id+"F5.boolean.opBoolean","INTERSECT",EDGE,{"derivedFrom":[makeQuery(id+"F1.opExtrude","SWEPT_FACE",FACE,{"disambiguationData":[OSD([sQuery(id+"F0.wireOp",EDGE,"E129")])]}),makeQuery(id+"F5.opRevolve","SWEPT_FACE",FACE,{"disambiguationData":[OSD([sQuery(id+"F4.wireOp",EDGE,"E149.filletArc")])]})]});
            var Q66;
            Q66=makeQuery(id+"F5.boolean.opBoolean","INTERSECT",EDGE,{"derivedFrom":[makeQuery(id+"F1.opExtrude","SWEPT_FACE",FACE,{"disambiguationData":[OSD([sQuery(id+"F0.wireOp",EDGE,"E137")])]}),makeQuery(id+"F5.opRevolve","SWEPT_FACE",FACE,{"disambiguationData":[OSD([sQuery(id+"F4.wireOp",EDGE,"E149.filletArc")])]})]});
            var Q67;
            Q67=makeQuery(id+"F5.boolean.opBoolean","INTERSECT",EDGE,{"derivedFrom":[makeQuery(id+"F1.opExtrude","SWEPT_FACE",FACE,{"disambiguationData":[OSD([sQuery(id+"F0.wireOp",EDGE,"E127")])]}),makeQuery(id+"F5.opRevolve","SWEPT_FACE",FACE,{"disambiguationData":[OSD([sQuery(id+"F4.wireOp",EDGE,"E149.filletArc")])]})]});
            var Q68;
            Q68=makeQuery(id+"F5.boolean.opBoolean","INTERSECT",EDGE,{"derivedFrom":[makeQuery(id+"F1.opExtrude","SWEPT_FACE",FACE,{"disambiguationData":[OSD([sQuery(id+"F0.wireOp",EDGE,"E135")])]}),makeQuery(id+"F5.opRevolve","SWEPT_FACE",FACE,{"disambiguationData":[OSD([sQuery(id+"F4.wireOp",EDGE,"E149.filletArc")])]})]});
            var Q69;
            Q69=makeQuery(id+"F5.boolean.opBoolean","INTERSECT",EDGE,{"derivedFrom":[makeQuery(id+"F1.opExtrude","SWEPT_FACE",FACE,{"disambiguationData":[OSD([sQuery(id+"F0.wireOp",EDGE,"E7")])]}),makeQuery(id+"F5.opRevolve","SWEPT_FACE",FACE,{"disambiguationData":[OSD([sQuery(id+"F4.wireOp",EDGE,"E149.filletArc")])]})]});
            var Q70;
            Q70=makeQuery(id+"F5.boolean.opBoolean","INTERSECT",EDGE,{"derivedFrom":[makeQuery(id+"F1.opExtrude","SWEPT_FACE",FACE,{"disambiguationData":[OSD([sQuery(id+"F0.wireOp",EDGE,"E143")])]}),makeQuery(id+"F5.opRevolve","SWEPT_FACE",FACE,{"disambiguationData":[OSD([sQuery(id+"F4.wireOp",EDGE,"E149.filletArc")])]})]});
            var Q71;
            Q71=makeQuery(id+"F5.boolean.opBoolean","INTERSECT",EDGE,{"derivedFrom":[makeQuery(id+"F1.opExtrude","SWEPT_FACE",FACE,{"disambiguationData":[OSD([sQuery(id+"F0.wireOp",EDGE,"E17")])]}),makeQuery(id+"F5.opRevolve","SWEPT_FACE",FACE,{"disambiguationData":[OSD([sQuery(id+"F4.wireOp",EDGE,"E149.filletArc")])]})]});
            var Q72;
            Q72=makeQuery(id+"F5.boolean.opBoolean","INTERSECT",EDGE,{"derivedFrom":[makeQuery(id+"F1.opExtrude","SWEPT_FACE",FACE,{"disambiguationData":[OSD([sQuery(id+"F0.wireOp",EDGE,"E9")])]}),makeQuery(id+"F5.opRevolve","SWEPT_FACE",FACE,{"disambiguationData":[OSD([sQuery(id+"F4.wireOp",EDGE,"E149.filletArc")])]})]});
            var Q73;
            Q73=makeQuery(id+"F5.boolean.opBoolean","INTERSECT",EDGE,{"derivedFrom":[makeQuery(id+"F1.opExtrude","SWEPT_FACE",FACE,{"disambiguationData":[OSD([sQuery(id+"F0.wireOp",EDGE,"E1")])]}),makeQuery(id+"F5.opRevolve","SWEPT_FACE",FACE,{"disambiguationData":[OSD([sQuery(id+"F4.wireOp",EDGE,"E149.filletArc")])]})]});
            var Q74;
            Q74=makeQuery(id+"F5.boolean.opBoolean","INTERSECT",EDGE,{"derivedFrom":[makeQuery(id+"F1.opExtrude","SWEPT_FACE",FACE,{"disambiguationData":[OSD([sQuery(id+"F0.wireOp",EDGE,"E124")])]}),makeQuery(id+"F5.opRevolve","SWEPT_FACE",FACE,{"disambiguationData":[OSD([sQuery(id+"F4.wireOp",EDGE,"E147.top")])]})]});
            var Q75;
            Q75=makeQuery(id+"F5.boolean.opBoolean","INTERSECT",EDGE,{"derivedFrom":[makeQuery(id+"F1.opExtrude","SWEPT_FACE",FACE,{"disambiguationData":[OSD([sQuery(id+"F0.wireOp",EDGE,"E132")])]}),makeQuery(id+"F5.opRevolve","SWEPT_FACE",FACE,{"disambiguationData":[OSD([sQuery(id+"F4.wireOp",EDGE,"E147.top")])]})]});
            var Q76;
            Q76=makeQuery(id+"F5.boolean.opBoolean","INTERSECT",EDGE,{"derivedFrom":[makeQuery(id+"F1.opExtrude","SWEPT_FACE",FACE,{"disambiguationData":[OSD([sQuery(id+"F0.wireOp",EDGE,"E124")])]}),makeQuery(id+"F5.opRevolve","SWEPT_FACE",FACE,{"disambiguationData":[OSD([sQuery(id+"F4.wireOp",EDGE,"E147.bottom")])]})]});
            var Q77;
            Q77=makeQuery(id+"F5.boolean.opBoolean","INTERSECT",EDGE,{"derivedFrom":[makeQuery(id+"F1.opExtrude","SWEPT_FACE",FACE,{"disambiguationData":[OSD([sQuery(id+"F0.wireOp",EDGE,"E116")])]}),makeQuery(id+"F5.opRevolve","SWEPT_FACE",FACE,{"disambiguationData":[OSD([sQuery(id+"F4.wireOp",EDGE,"E147.top")])]})]});
            var Q78;
            Q78=makeQuery(id+"F5.boolean.opBoolean","INTERSECT",EDGE,{"derivedFrom":[makeQuery(id+"F1.opExtrude","SWEPT_FACE",FACE,{"disambiguationData":[OSD([sQuery(id+"F0.wireOp",EDGE,"E116")])]}),makeQuery(id+"F5.opRevolve","SWEPT_FACE",FACE,{"disambiguationData":[OSD([sQuery(id+"F4.wireOp",EDGE,"E147.bottom")])]})]});
            var Q79;
            Q79=makeQuery(id+"F5.boolean.opBoolean","INTERSECT",EDGE,{"derivedFrom":[makeQuery(id+"F1.opExtrude","SWEPT_FACE",FACE,{"disambiguationData":[OSD([sQuery(id+"F0.wireOp",EDGE,"E108")])]}),makeQuery(id+"F5.opRevolve","SWEPT_FACE",FACE,{"disambiguationData":[OSD([sQuery(id+"F4.wireOp",EDGE,"E147.top")])]})]});
            var Q80;
            Q80=makeQuery(id+"F5.boolean.opBoolean","INTERSECT",EDGE,{"derivedFrom":[makeQuery(id+"F1.opExtrude","SWEPT_FACE",FACE,{"disambiguationData":[OSD([sQuery(id+"F0.wireOp",EDGE,"E108")])]}),makeQuery(id+"F5.opRevolve","SWEPT_FACE",FACE,{"disambiguationData":[OSD([sQuery(id+"F4.wireOp",EDGE,"E147.bottom")])]})]});
            var Q81;
            Q81=makeQuery(id+"F1.opExtrude","CAP_EDGE",EDGE,{"disambiguationData":[OSD([sQuery(id+"F0.wireOp",EDGE,"E72")])],"isStart":false});
            var Q82;
            Q82=makeQuery(id+"F1.opExtrude","CAP_EDGE",EDGE,{"disambiguationData":[OSD([sQuery(id+"F0.wireOp",EDGE,"E64")])],"isStart":false});
            var Q83;
            Q83=makeQuery(id+"F1.opExtrude","CAP_EDGE",EDGE,{"disambiguationData":[OSD([sQuery(id+"F0.wireOp",EDGE,"E56")])],"isStart":false});
            var Q84;
            Q84=makeQuery(id+"F5.boolean.opBoolean","INTERSECT",EDGE,{"derivedFrom":[makeQuery(id+"F1.opExtrude","SWEPT_FACE",FACE,{"disambiguationData":[OSD([sQuery(id+"F0.wireOp",EDGE,"E55")])]}),makeQuery(id+"F5.opRevolve","SWEPT_FACE",FACE,{"disambiguationData":[OSD([sQuery(id+"F4.wireOp",EDGE,"E149.filletArc")])]})]});
            var Q85;
            Q85=makeQuery(id+"F5.boolean.opBoolean","INTERSECT",EDGE,{"derivedFrom":[makeQuery(id+"F1.opExtrude","SWEPT_FACE",FACE,{"disambiguationData":[OSD([sQuery(id+"F0.wireOp",EDGE,"E47")])]}),makeQuery(id+"F5.opRevolve","SWEPT_FACE",FACE,{"disambiguationData":[OSD([sQuery(id+"F4.wireOp",EDGE,"E149.filletArc")])]})]});
            var Q86;
            Q86=makeQuery(id+"F5.boolean.opBoolean","INTERSECT",EDGE,{"derivedFrom":[makeQuery(id+"F1.opExtrude","SWEPT_FACE",FACE,{"disambiguationData":[OSD([sQuery(id+"F0.wireOp",EDGE,"E63")])]}),makeQuery(id+"F5.opRevolve","SWEPT_FACE",FACE,{"disambiguationData":[OSD([sQuery(id+"F4.wireOp",EDGE,"E149.filletArc")])]})]});
            var Q87;
            Q87=makeQuery(id+"F5.boolean.opBoolean","INTERSECT",EDGE,{"derivedFrom":[makeQuery(id+"F1.opExtrude","SWEPT_FACE",FACE,{"disambiguationData":[OSD([sQuery(id+"F0.wireOp",EDGE,"E71")])]}),makeQuery(id+"F5.opRevolve","SWEPT_FACE",FACE,{"disambiguationData":[OSD([sQuery(id+"F4.wireOp",EDGE,"E149.filletArc")])]})]});
            var Q88;
            Q88=makeQuery(id+"F1.opExtrude","CAP_EDGE",EDGE,{"disambiguationData":[OSD([sQuery(id+"F0.wireOp",EDGE,"E16")])],"isStart":false});
            var Q89;
            Q89=makeQuery(id+"F1.opExtrude","CAP_EDGE",EDGE,{"disambiguationData":[OSD([sQuery(id+"F0.wireOp",EDGE,"E24")])],"isStart":false});
            var Q90;
            Q90=makeQuery(id+"F1.opExtrude","CAP_EDGE",EDGE,{"disambiguationData":[OSD([sQuery(id+"F0.wireOp",EDGE,"E32")])],"isStart":false});
            var Q91;
            Q91=makeQuery(id+"F1.opExtrude","CAP_EDGE",EDGE,{"disambiguationData":[OSD([sQuery(id+"F0.wireOp",EDGE,"E40")])],"isStart":false});
            var Q92;
            Q92=makeQuery(id+"F1.opExtrude","CAP_EDGE",EDGE,{"disambiguationData":[OSD([sQuery(id+"F0.wireOp",EDGE,"E48")])],"isStart":false});
            var Q93;
            Q93=makeQuery(id+"F1.opExtrude","CAP_EDGE",EDGE,{"disambiguationData":[OSD([sQuery(id+"F0.wireOp",EDGE,"E80")])],"isStart":false});
            var Q94;
            Q94=makeQuery(id+"F1.opExtrude","CAP_EDGE",EDGE,{"disambiguationData":[OSD([sQuery(id+"F0.wireOp",EDGE,"E88")])],"isStart":false});
            var Q95;
            Q95=makeQuery(id+"F1.opExtrude","CAP_EDGE",EDGE,{"disambiguationData":[OSD([sQuery(id+"F0.wireOp",EDGE,"E96")])],"isStart":false});
            var Q96;
            Q96=makeQuery(id+"F1.opExtrude","CAP_EDGE",EDGE,{"disambiguationData":[OSD([sQuery(id+"F0.wireOp",EDGE,"E104")])],"isStart":false});
            var Q97;
            Q97=makeQuery(id+"F1.opExtrude","CAP_EDGE",EDGE,{"disambiguationData":[OSD([sQuery(id+"F0.wireOp",EDGE,"E112")])],"isStart":false});
            var Q98;
            Q98=makeQuery(id+"F1.opExtrude","CAP_EDGE",EDGE,{"disambiguationData":[OSD([sQuery(id+"F0.wireOp",EDGE,"E120")])],"isStart":false});
            var Q99;
            Q99=makeQuery(id+"F1.opExtrude","CAP_EDGE",EDGE,{"disambiguationData":[OSD([sQuery(id+"F0.wireOp",EDGE,"E128")])],"isStart":false});
            var Q100;
            Q100=makeQuery(id+"F1.opExtrude","CAP_EDGE",EDGE,{"disambiguationData":[OSD([sQuery(id+"F0.wireOp",EDGE,"E136")])],"isStart":false});
            var Q101;
            Q101=makeQuery(id+"F1.opExtrude","CAP_EDGE",EDGE,{"disambiguationData":[OSD([sQuery(id+"F0.wireOp",EDGE,"E144")])],"isStart":false});
            var Q102;
            Q102=makeQuery(id+"F1.opExtrude","CAP_EDGE",EDGE,{"disambiguationData":[OSD([sQuery(id+"F0.wireOp",EDGE,"E8")])],"isStart":false});
            var Q103;
            Q103=makeQuery(id+"F1.opExtrude","CAP_EDGE",EDGE,{"disambiguationData":[OSD([sQuery(id+"F0.wireOp",EDGE,"E82")])],"isStart":true});
            var Q104;
            Q104=makeQuery(id+"F1.opExtrude","CAP_EDGE",EDGE,{"disambiguationData":[OSD([sQuery(id+"F0.wireOp",EDGE,"E90")])],"isStart":true});
            var Q105;
            Q105=makeQuery(id+"F1.opExtrude","CAP_EDGE",EDGE,{"disambiguationData":[OSD([sQuery(id+"F0.wireOp",EDGE,"E98")])],"isStart":true});
            var Q106;
            Q106=makeQuery(id+"F1.opExtrude","CAP_EDGE",EDGE,{"disambiguationData":[OSD([sQuery(id+"F0.wireOp",EDGE,"E106")])],"isStart":true});
            var Q107;
            Q107=makeQuery(id+"F1.opExtrude","CAP_EDGE",EDGE,{"disambiguationData":[OSD([sQuery(id+"F0.wireOp",EDGE,"E114")])],"isStart":true});
            var Q108;
            Q108=makeQuery(id+"F1.opExtrude","CAP_EDGE",EDGE,{"disambiguationData":[OSD([sQuery(id+"F0.wireOp",EDGE,"E122")])],"isStart":true});
            var Q109;
            Q109=makeQuery(id+"F1.opExtrude","CAP_EDGE",EDGE,{"disambiguationData":[OSD([sQuery(id+"F0.wireOp",EDGE,"E130")])],"isStart":true});
            var Q110;
            Q110=makeQuery(id+"F1.opExtrude","CAP_EDGE",EDGE,{"disambiguationData":[OSD([sQuery(id+"F0.wireOp",EDGE,"E138")])],"isStart":true});
            var Q111;
            Q111=makeQuery(id+"F1.opExtrude","CAP_EDGE",EDGE,{"disambiguationData":[OSD([sQuery(id+"F0.wireOp",EDGE,"E2")])],"isStart":true});
            var Q112;
            Q112=makeQuery(id+"F1.opExtrude","CAP_EDGE",EDGE,{"disambiguationData":[OSD([sQuery(id+"F0.wireOp",EDGE,"E10")])],"isStart":true});
            var Q113;
            Q113=makeQuery(id+"F1.opExtrude","CAP_EDGE",EDGE,{"disambiguationData":[OSD([sQuery(id+"F0.wireOp",EDGE,"E18")])],"isStart":true});
            var Q114;
            Q114=makeQuery(id+"F1.opExtrude","CAP_EDGE",EDGE,{"disambiguationData":[OSD([sQuery(id+"F0.wireOp",EDGE,"E26")])],"isStart":true});
            var Q115;
            Q115=makeQuery(id+"F1.opExtrude","CAP_EDGE",EDGE,{"disambiguationData":[OSD([sQuery(id+"F0.wireOp",EDGE,"E34")])],"isStart":true});
            var Q116;
            Q116=makeQuery(id+"F1.opExtrude","CAP_EDGE",EDGE,{"disambiguationData":[OSD([sQuery(id+"F0.wireOp",EDGE,"E22")])],"isStart":true});
            var Q117;
            Q117=makeQuery(id+"F1.opExtrude","CAP_EDGE",EDGE,{"disambiguationData":[OSD([sQuery(id+"F0.wireOp",EDGE,"E30")])],"isStart":true});
            var Q118;
            Q118=makeQuery(id+"F1.opExtrude","CAP_EDGE",EDGE,{"disambiguationData":[OSD([sQuery(id+"F0.wireOp",EDGE,"E38")])],"isStart":true});
            var Q119;
            Q119=makeQuery(id+"F1.opExtrude","CAP_EDGE",EDGE,{"disambiguationData":[OSD([sQuery(id+"F0.wireOp",EDGE,"E46")])],"isStart":true});
            var Q120;
            Q120=makeQuery(id+"F1.opExtrude","CAP_EDGE",EDGE,{"disambiguationData":[OSD([sQuery(id+"F0.wireOp",EDGE,"E54")])],"isStart":true});
            var Q121;
            Q121=makeQuery(id+"F1.opExtrude","CAP_EDGE",EDGE,{"disambiguationData":[OSD([sQuery(id+"F0.wireOp",EDGE,"E62")])],"isStart":true});
            var Q122;
            Q122=makeQuery(id+"F1.opExtrude","CAP_EDGE",EDGE,{"disambiguationData":[OSD([sQuery(id+"F0.wireOp",EDGE,"E70")])],"isStart":true});
            var Q123;
            Q123=makeQuery(id+"F1.opExtrude","CAP_EDGE",EDGE,{"disambiguationData":[OSD([sQuery(id+"F0.wireOp",EDGE,"E78")])],"isStart":true});
            var Q124;
            Q124=makeQuery(id+"F1.opExtrude","CAP_EDGE",EDGE,{"disambiguationData":[OSD([sQuery(id+"F0.wireOp",EDGE,"E86")])],"isStart":true});
            var Q125;
            Q125=makeQuery(id+"F1.opExtrude","CAP_EDGE",EDGE,{"disambiguationData":[OSD([sQuery(id+"F0.wireOp",EDGE,"E94")])],"isStart":true});
            var Q126;
            Q126=makeQuery(id+"F1.opExtrude","CAP_EDGE",EDGE,{"disambiguationData":[OSD([sQuery(id+"F0.wireOp",EDGE,"E102")])],"isStart":true});
            var Q127;
            Q127=makeQuery(id+"F1.opExtrude","CAP_EDGE",EDGE,{"disambiguationData":[OSD([sQuery(id+"F0.wireOp",EDGE,"E110")])],"isStart":true});
            var Q128;
            Q128=makeQuery(id+"F1.opExtrude","CAP_EDGE",EDGE,{"disambiguationData":[OSD([sQuery(id+"F0.wireOp",EDGE,"E118")])],"isStart":true});
            var Q129;
            Q129=makeQuery(id+"F1.opExtrude","CAP_EDGE",EDGE,{"disambiguationData":[OSD([sQuery(id+"F0.wireOp",EDGE,"E126")])],"isStart":true});
            var Q130;
            Q130=makeQuery(id+"F1.opExtrude","CAP_EDGE",EDGE,{"disambiguationData":[OSD([sQuery(id+"F0.wireOp",EDGE,"E134")])],"isStart":true});
            var Q131;
            Q131=makeQuery(id+"F1.opExtrude","CAP_EDGE",EDGE,{"disambiguationData":[OSD([sQuery(id+"F0.wireOp",EDGE,"E142")])],"isStart":true});
            var Q132;
            Q132=makeQuery(id+"F1.opExtrude","CAP_EDGE",EDGE,{"disambiguationData":[OSD([sQuery(id+"F0.wireOp",EDGE,"E6")])],"isStart":true});
            var Q133;
            Q133=makeQuery(id+"F1.opExtrude","CAP_EDGE",EDGE,{"disambiguationData":[OSD([sQuery(id+"F0.wireOp",EDGE,"E74")])],"isStart":true});
            var Q134;
            Q134=makeQuery(id+"F1.opExtrude","CAP_EDGE",EDGE,{"disambiguationData":[OSD([sQuery(id+"F0.wireOp",EDGE,"E66")])],"isStart":true});
            var Q135;
            Q135=makeQuery(id+"F1.opExtrude","CAP_EDGE",EDGE,{"disambiguationData":[OSD([sQuery(id+"F0.wireOp",EDGE,"E42")])],"isStart":true});
            var Q136;
            Q136=makeQuery(id+"F1.opExtrude","CAP_EDGE",EDGE,{"disambiguationData":[OSD([sQuery(id+"F0.wireOp",EDGE,"E14")])],"isStart":true});
            var Q137;
            Q137=makeQuery(id+"F1.opExtrude","CAP_EDGE",EDGE,{"disambiguationData":[OSD([sQuery(id+"F0.wireOp",EDGE,"E28")])],"isStart":true});
            var Q138;
            Q138=makeQuery(id+"F1.opExtrude","CAP_EDGE",EDGE,{"disambiguationData":[OSD([sQuery(id+"F0.wireOp",EDGE,"E20")])],"isStart":true});
            var Q139;
            Q139=makeQuery(id+"F1.opExtrude","CAP_EDGE",EDGE,{"disambiguationData":[OSD([sQuery(id+"F0.wireOp",EDGE,"E12")])],"isStart":true});
            var Q140;
            Q140=makeQuery(id+"F1.opExtrude","CAP_EDGE",EDGE,{"disambiguationData":[OSD([sQuery(id+"F0.wireOp",EDGE,"E4")])],"isStart":true});
            var Q141;
            Q141=makeQuery(id+"F1.opExtrude","CAP_EDGE",EDGE,{"disambiguationData":[OSD([sQuery(id+"F0.wireOp",EDGE,"E36")])],"isStart":true});
            var Q142;
            Q142=makeQuery(id+"F1.opExtrude","CAP_EDGE",EDGE,{"disambiguationData":[OSD([sQuery(id+"F0.wireOp",EDGE,"E44")])],"isStart":true});
            var Q143;
            Q143=makeQuery(id+"F1.opExtrude","CAP_EDGE",EDGE,{"disambiguationData":[OSD([sQuery(id+"F0.wireOp",EDGE,"E52")])],"isStart":true});
            var Q144;
            Q144=makeQuery(id+"F1.opExtrude","CAP_EDGE",EDGE,{"disambiguationData":[OSD([sQuery(id+"F0.wireOp",EDGE,"E60")])],"isStart":true});
            var Q145;
            Q145=makeQuery(id+"F1.opExtrude","CAP_EDGE",EDGE,{"disambiguationData":[OSD([sQuery(id+"F0.wireOp",EDGE,"E68")])],"isStart":true});
            var Q146;
            Q146=makeQuery(id+"F1.opExtrude","CAP_EDGE",EDGE,{"disambiguationData":[OSD([sQuery(id+"F0.wireOp",EDGE,"E76")])],"isStart":true});
            var Q147;
            Q147=makeQuery(id+"F1.opExtrude","CAP_EDGE",EDGE,{"disambiguationData":[OSD([sQuery(id+"F0.wireOp",EDGE,"E84")])],"isStart":true});
            var Q148;
            Q148=makeQuery(id+"F1.opExtrude","CAP_EDGE",EDGE,{"disambiguationData":[OSD([sQuery(id+"F0.wireOp",EDGE,"E92")])],"isStart":true});
            var Q149;
            Q149=makeQuery(id+"F1.opExtrude","CAP_EDGE",EDGE,{"disambiguationData":[OSD([sQuery(id+"F0.wireOp",EDGE,"E100")])],"isStart":true});
            var Q150;
            Q150=makeQuery(id+"F1.opExtrude","CAP_EDGE",EDGE,{"disambiguationData":[OSD([sQuery(id+"F0.wireOp",EDGE,"E108")])],"isStart":true});
            var Q151;
            Q151=makeQuery(id+"F1.opExtrude","CAP_EDGE",EDGE,{"disambiguationData":[OSD([sQuery(id+"F0.wireOp",EDGE,"E116")])],"isStart":true});
            var Q152;
            Q152=makeQuery(id+"F1.opExtrude","CAP_EDGE",EDGE,{"disambiguationData":[OSD([sQuery(id+"F0.wireOp",EDGE,"E124")])],"isStart":true});
            var Q153;
            Q153=makeQuery(id+"F1.opExtrude","CAP_EDGE",EDGE,{"disambiguationData":[OSD([sQuery(id+"F0.wireOp",EDGE,"E132")])],"isStart":true});
            var Q154;
            Q154=makeQuery(id+"F1.opExtrude","CAP_EDGE",EDGE,{"disambiguationData":[OSD([sQuery(id+"F0.wireOp",EDGE,"E140")])],"isStart":true});
            var Q155;
            Q155=makeQuery(id+"F1.opExtrude","CAP_EDGE",EDGE,{"disambiguationData":[OSD([sQuery(id+"F0.wireOp",EDGE,"E58")])],"isStart":true});
            var Q156;
            Q156=makeQuery(id+"F1.opExtrude","CAP_EDGE",EDGE,{"disambiguationData":[OSD([sQuery(id+"F0.wireOp",EDGE,"E50")])],"isStart":true});
            var Q157;
            Q157=makeQuery(id+"F1.opExtrude","CAP_EDGE",EDGE,{"disambiguationData":[OSD([sQuery(id+"F0.wireOp",EDGE,"E56")])],"isStart":true});
            var Q158;
            Q158=makeQuery(id+"F1.opExtrude","CAP_EDGE",EDGE,{"disambiguationData":[OSD([sQuery(id+"F0.wireOp",EDGE,"E64")])],"isStart":true});
            var Q159;
            Q159=makeQuery(id+"F1.opExtrude","CAP_EDGE",EDGE,{"disambiguationData":[OSD([sQuery(id+"F0.wireOp",EDGE,"E72")])],"isStart":true});
            var Q160;
            Q160=makeQuery(id+"F1.opExtrude","CAP_EDGE",EDGE,{"disambiguationData":[OSD([sQuery(id+"F0.wireOp",EDGE,"E80")])],"isStart":true});
            var Q161;
            Q161=makeQuery(id+"F1.opExtrude","CAP_EDGE",EDGE,{"disambiguationData":[OSD([sQuery(id+"F0.wireOp",EDGE,"E88")])],"isStart":true});
            var Q162;
            Q162=makeQuery(id+"F1.opExtrude","CAP_EDGE",EDGE,{"disambiguationData":[OSD([sQuery(id+"F0.wireOp",EDGE,"E96")])],"isStart":true});
            var Q163;
            Q163=makeQuery(id+"F1.opExtrude","CAP_EDGE",EDGE,{"disambiguationData":[OSD([sQuery(id+"F0.wireOp",EDGE,"E104")])],"isStart":true});
            var Q164;
            Q164=makeQuery(id+"F1.opExtrude","CAP_EDGE",EDGE,{"disambiguationData":[OSD([sQuery(id+"F0.wireOp",EDGE,"E112")])],"isStart":true});
            var Q165;
            Q165=makeQuery(id+"F1.opExtrude","CAP_EDGE",EDGE,{"disambiguationData":[OSD([sQuery(id+"F0.wireOp",EDGE,"E120")])],"isStart":true});
            var Q166;
            Q166=makeQuery(id+"F1.opExtrude","CAP_EDGE",EDGE,{"disambiguationData":[OSD([sQuery(id+"F0.wireOp",EDGE,"E128")])],"isStart":true});
            var Q167;
            Q167=makeQuery(id+"F1.opExtrude","CAP_EDGE",EDGE,{"disambiguationData":[OSD([sQuery(id+"F0.wireOp",EDGE,"E136")])],"isStart":true});
            var Q168;
            Q168=makeQuery(id+"F1.opExtrude","CAP_EDGE",EDGE,{"disambiguationData":[OSD([sQuery(id+"F0.wireOp",EDGE,"E144")])],"isStart":true});
            var Q169;
            Q169=makeQuery(id+"F1.opExtrude","CAP_EDGE",EDGE,{"disambiguationData":[OSD([sQuery(id+"F0.wireOp",EDGE,"E40")])],"isStart":true});
            var Q170;
            Q170=makeQuery(id+"F1.opExtrude","CAP_EDGE",EDGE,{"disambiguationData":[OSD([sQuery(id+"F0.wireOp",EDGE,"E48")])],"isStart":true});
            var Q171;
            Q171=makeQuery(id+"F1.opExtrude","CAP_EDGE",EDGE,{"disambiguationData":[OSD([sQuery(id+"F0.wireOp",EDGE,"E32")])],"isStart":true});
            var Q172;
            Q172=makeQuery(id+"F1.opExtrude","CAP_EDGE",EDGE,{"disambiguationData":[OSD([sQuery(id+"F0.wireOp",EDGE,"E24")])],"isStart":true});
            var Q173;
            Q173=makeQuery(id+"F1.opExtrude","CAP_EDGE",EDGE,{"disambiguationData":[OSD([sQuery(id+"F0.wireOp",EDGE,"E16")])],"isStart":true});
            var Q174;
            Q174=makeQuery(id+"F1.opExtrude","CAP_EDGE",EDGE,{"disambiguationData":[OSD([sQuery(id+"F0.wireOp",EDGE,"E8")])],"isStart":true});
            var Q175;
            Q175=makeQuery(id+"F5.boolean.opBoolean","INTERSECT",EDGE,{"derivedFrom":[makeQuery(id+"F1.opExtrude","SWEPT_FACE",FACE,{"disambiguationData":[OSD([sQuery(id+"F0.wireOp",EDGE,"E74")])]}),makeQuery(id+"F5.opRevolve","SWEPT_FACE",FACE,{"disambiguationData":[OSD([sQuery(id+"F4.wireOp",EDGE,"E147.bottom")])]})]});
            var Q176;
            Q176=makeQuery(id+"F5.boolean.opBoolean","INTERSECT",EDGE,{"derivedFrom":[makeQuery(id+"F1.opExtrude","SWEPT_FACE",FACE,{"disambiguationData":[OSD([sQuery(id+"F0.wireOp",EDGE,"E66")])]}),makeQuery(id+"F5.opRevolve","SWEPT_FACE",FACE,{"disambiguationData":[OSD([sQuery(id+"F4.wireOp",EDGE,"E147.bottom")])]})]});
            var Q177;
            Q177=makeQuery(id+"F5.boolean.opBoolean","INTERSECT",EDGE,{"derivedFrom":[makeQuery(id+"F1.opExtrude","SWEPT_FACE",FACE,{"disambiguationData":[OSD([sQuery(id+"F0.wireOp",EDGE,"E58")])]}),makeQuery(id+"F5.opRevolve","SWEPT_FACE",FACE,{"disambiguationData":[OSD([sQuery(id+"F4.wireOp",EDGE,"E147.bottom")])]})]});
            var Q178;
            Q178=makeQuery(id+"F5.boolean.opBoolean","INTERSECT",EDGE,{"derivedFrom":[makeQuery(id+"F1.opExtrude","SWEPT_FACE",FACE,{"disambiguationData":[OSD([sQuery(id+"F0.wireOp",EDGE,"E50")])]}),makeQuery(id+"F5.opRevolve","SWEPT_FACE",FACE,{"disambiguationData":[OSD([sQuery(id+"F4.wireOp",EDGE,"E147.bottom")])]})]});
            var Q179;
            Q179=makeQuery(id+"F5.boolean.opBoolean","INTERSECT",EDGE,{"derivedFrom":[makeQuery(id+"F1.opExtrude","SWEPT_FACE",FACE,{"disambiguationData":[OSD([sQuery(id+"F0.wireOp",EDGE,"E34")])]}),makeQuery(id+"F5.opRevolve","SWEPT_FACE",FACE,{"disambiguationData":[OSD([sQuery(id+"F4.wireOp",EDGE,"E147.bottom")])]})]});
            var Q180;
            Q180=makeQuery(id+"F5.boolean.opBoolean","INTERSECT",EDGE,{"derivedFrom":[makeQuery(id+"F1.opExtrude","SWEPT_FACE",FACE,{"disambiguationData":[OSD([sQuery(id+"F0.wireOp",EDGE,"E26")])]}),makeQuery(id+"F5.opRevolve","SWEPT_FACE",FACE,{"disambiguationData":[OSD([sQuery(id+"F4.wireOp",EDGE,"E147.bottom")])]})]});
            var Q181;
            Q181=makeQuery(id+"F5.boolean.opBoolean","INTERSECT",EDGE,{"derivedFrom":[makeQuery(id+"F1.opExtrude","SWEPT_FACE",FACE,{"disambiguationData":[OSD([sQuery(id+"F0.wireOp",EDGE,"E38")])]}),makeQuery(id+"F5.opRevolve","SWEPT_FACE",FACE,{"disambiguationData":[OSD([sQuery(id+"F4.wireOp",EDGE,"E147.bottom")])]})]});
            var Q182;
            Q182=makeQuery(id+"F5.boolean.opBoolean","INTERSECT",EDGE,{"derivedFrom":[makeQuery(id+"F1.opExtrude","SWEPT_FACE",FACE,{"disambiguationData":[OSD([sQuery(id+"F0.wireOp",EDGE,"E38")])]}),makeQuery(id+"F5.opRevolve","SWEPT_FACE",FACE,{"disambiguationData":[OSD([sQuery(id+"F4.wireOp",EDGE,"E147.top")])]})]});
            var Q183;
            Q183=makeQuery(id+"F5.boolean.opBoolean","INTERSECT",EDGE,{"derivedFrom":[makeQuery(id+"F1.opExtrude","SWEPT_FACE",FACE,{"disambiguationData":[OSD([sQuery(id+"F0.wireOp",EDGE,"E42")])]}),makeQuery(id+"F5.opRevolve","SWEPT_FACE",FACE,{"disambiguationData":[OSD([sQuery(id+"F4.wireOp",EDGE,"E147.top")])]})]});
            var Q184;
            Q184=makeQuery(id+"F5.boolean.opBoolean","INTERSECT",EDGE,{"derivedFrom":[makeQuery(id+"F1.opExtrude","SWEPT_FACE",FACE,{"disambiguationData":[OSD([sQuery(id+"F0.wireOp",EDGE,"E22")])]}),makeQuery(id+"F5.opRevolve","SWEPT_FACE",FACE,{"disambiguationData":[OSD([sQuery(id+"F4.wireOp",EDGE,"E147.top")])]})]});
            var Q185;
            Q185=makeQuery(id+"F5.boolean.opBoolean","INTERSECT",EDGE,{"derivedFrom":[makeQuery(id+"F1.opExtrude","SWEPT_FACE",FACE,{"disambiguationData":[OSD([sQuery(id+"F0.wireOp",EDGE,"E22")])]}),makeQuery(id+"F5.opRevolve","SWEPT_FACE",FACE,{"disambiguationData":[OSD([sQuery(id+"F4.wireOp",EDGE,"E147.bottom")])]})]});
            var Q186;
            Q186=makeQuery(id+"F5.boolean.opBoolean","INTERSECT",EDGE,{"derivedFrom":[makeQuery(id+"F1.opExtrude","SWEPT_FACE",FACE,{"disambiguationData":[OSD([sQuery(id+"F0.wireOp",EDGE,"E14")])]}),makeQuery(id+"F5.opRevolve","SWEPT_FACE",FACE,{"disambiguationData":[OSD([sQuery(id+"F4.wireOp",EDGE,"E147.top")])]})]});
            var Q187;
            Q187=makeQuery(id+"F5.boolean.opBoolean","INTERSECT",EDGE,{"derivedFrom":[makeQuery(id+"F1.opExtrude","SWEPT_FACE",FACE,{"disambiguationData":[OSD([sQuery(id+"F0.wireOp",EDGE,"E14")])]}),makeQuery(id+"F5.opRevolve","SWEPT_FACE",FACE,{"disambiguationData":[OSD([sQuery(id+"F4.wireOp",EDGE,"E147.bottom")])]})]});
            var Q188;
            Q188=makeQuery(id+"F5.boolean.opBoolean","INTERSECT",EDGE,{"derivedFrom":[makeQuery(id+"F1.opExtrude","SWEPT_FACE",FACE,{"disambiguationData":[OSD([sQuery(id+"F0.wireOp",EDGE,"E12")])]}),makeQuery(id+"F5.opRevolve","SWEPT_FACE",FACE,{"disambiguationData":[OSD([sQuery(id+"F4.wireOp",EDGE,"E147.top")])]})]});
            var Q189;
            Q189=makeQuery(id+"F5.boolean.opBoolean","INTERSECT",EDGE,{"derivedFrom":[makeQuery(id+"F1.opExtrude","SWEPT_FACE",FACE,{"disambiguationData":[OSD([sQuery(id+"F0.wireOp",EDGE,"E12")])]}),makeQuery(id+"F5.opRevolve","SWEPT_FACE",FACE,{"disambiguationData":[OSD([sQuery(id+"F4.wireOp",EDGE,"E147.bottom")])]})]});
            var Q190;
            Q190=makeQuery(id+"F5.boolean.opBoolean","INTERSECT",EDGE,{"derivedFrom":[makeQuery(id+"F1.opExtrude","SWEPT_FACE",FACE,{"disambiguationData":[OSD([sQuery(id+"F0.wireOp",EDGE,"E4")])]}),makeQuery(id+"F5.opRevolve","SWEPT_FACE",FACE,{"disambiguationData":[OSD([sQuery(id+"F4.wireOp",EDGE,"E147.top")])]})]});
            var Q191;
            Q191=makeQuery(id+"F5.boolean.opBoolean","INTERSECT",EDGE,{"derivedFrom":[makeQuery(id+"F1.opExtrude","SWEPT_FACE",FACE,{"disambiguationData":[OSD([sQuery(id+"F0.wireOp",EDGE,"E4")])]}),makeQuery(id+"F5.opRevolve","SWEPT_FACE",FACE,{"disambiguationData":[OSD([sQuery(id+"F4.wireOp",EDGE,"E147.bottom")])]})]});
            var Q192;
            Q192=makeQuery(id+"F5.boolean.opBoolean","INTERSECT",EDGE,{"derivedFrom":[makeQuery(id+"F1.opExtrude","SWEPT_FACE",FACE,{"disambiguationData":[OSD([sQuery(id+"F0.wireOp",EDGE,"E140")])]}),makeQuery(id+"F5.opRevolve","SWEPT_FACE",FACE,{"disambiguationData":[OSD([sQuery(id+"F4.wireOp",EDGE,"E147.top")])]})]});
            var Q193;
            Q193=makeQuery(id+"F5.boolean.opBoolean","INTERSECT",EDGE,{"derivedFrom":[makeQuery(id+"F1.opExtrude","SWEPT_FACE",FACE,{"disambiguationData":[OSD([sQuery(id+"F0.wireOp",EDGE,"E140")])]}),makeQuery(id+"F5.opRevolve","SWEPT_FACE",FACE,{"disambiguationData":[OSD([sQuery(id+"F4.wireOp",EDGE,"E147.bottom")])]})]});
            var Q194;
            Q194=makeQuery(id+"F5.boolean.opBoolean","INTERSECT",EDGE,{"derivedFrom":[makeQuery(id+"F1.opExtrude","SWEPT_FACE",FACE,{"disambiguationData":[OSD([sQuery(id+"F0.wireOp",EDGE,"E92")])]}),makeQuery(id+"F5.opRevolve","SWEPT_FACE",FACE,{"disambiguationData":[OSD([sQuery(id+"F4.wireOp",EDGE,"E147.top")])]})]});
            var Q195;
            Q195=makeQuery(id+"F5.boolean.opBoolean","INTERSECT",EDGE,{"derivedFrom":[makeQuery(id+"F1.opExtrude","SWEPT_FACE",FACE,{"disambiguationData":[OSD([sQuery(id+"F0.wireOp",EDGE,"E92")])]}),makeQuery(id+"F5.opRevolve","SWEPT_FACE",FACE,{"disambiguationData":[OSD([sQuery(id+"F4.wireOp",EDGE,"E147.bottom")])]})]});
            var Q196;
            Q196=makeQuery(id+"F5.boolean.opBoolean","INTERSECT",EDGE,{"derivedFrom":[makeQuery(id+"F1.opExtrude","SWEPT_FACE",FACE,{"disambiguationData":[OSD([sQuery(id+"F0.wireOp",EDGE,"E100")])]}),makeQuery(id+"F5.opRevolve","SWEPT_FACE",FACE,{"disambiguationData":[OSD([sQuery(id+"F4.wireOp",EDGE,"E147.bottom")])]})]});
            var Q197;
            Q197=makeQuery(id+"F5.boolean.opBoolean","INTERSECT",EDGE,{"derivedFrom":[makeQuery(id+"F1.opExtrude","SWEPT_FACE",FACE,{"disambiguationData":[OSD([sQuery(id+"F0.wireOp",EDGE,"E100")])]}),makeQuery(id+"F5.opRevolve","SWEPT_FACE",FACE,{"disambiguationData":[OSD([sQuery(id+"F4.wireOp",EDGE,"E147.top")])]})]});
            var Q198;
            Q198=makeQuery(id+"F5.boolean.opBoolean","INTERSECT",EDGE,{"derivedFrom":[makeQuery(id+"F1.opExtrude","SWEPT_FACE",FACE,{"disambiguationData":[OSD([sQuery(id+"F0.wireOp",EDGE,"E84")])]}),makeQuery(id+"F5.opRevolve","SWEPT_FACE",FACE,{"disambiguationData":[OSD([sQuery(id+"F4.wireOp",EDGE,"E147.bottom")])]})]});
            var Q199;
            Q199=makeQuery(id+"F5.boolean.opBoolean","INTERSECT",EDGE,{"derivedFrom":[makeQuery(id+"F1.opExtrude","SWEPT_FACE",FACE,{"disambiguationData":[OSD([sQuery(id+"F0.wireOp",EDGE,"E84")])]}),makeQuery(id+"F5.opRevolve","SWEPT_FACE",FACE,{"disambiguationData":[OSD([sQuery(id+"F4.wireOp",EDGE,"E147.top")])]})]});
            var Q200;
            Q200=makeQuery(id+"F5.boolean.opBoolean","INTERSECT",EDGE,{"derivedFrom":[makeQuery(id+"F1.opExtrude","SWEPT_FACE",FACE,{"disambiguationData":[OSD([sQuery(id+"F0.wireOp",EDGE,"E76")])]}),makeQuery(id+"F5.opRevolve","SWEPT_FACE",FACE,{"disambiguationData":[OSD([sQuery(id+"F4.wireOp",EDGE,"E147.top")])]})]});
            var Q201;
            Q201=makeQuery(id+"F5.boolean.opBoolean","INTERSECT",EDGE,{"derivedFrom":[makeQuery(id+"F1.opExtrude","SWEPT_FACE",FACE,{"disambiguationData":[OSD([sQuery(id+"F0.wireOp",EDGE,"E76")])]}),makeQuery(id+"F5.opRevolve","SWEPT_FACE",FACE,{"disambiguationData":[OSD([sQuery(id+"F4.wireOp",EDGE,"E147.bottom")])]})]});
            var Q202;
            Q202=makeQuery(id+"F5.boolean.opBoolean","INTERSECT",EDGE,{"derivedFrom":[makeQuery(id+"F1.opExtrude","SWEPT_FACE",FACE,{"disambiguationData":[OSD([sQuery(id+"F0.wireOp",EDGE,"E68")])]}),makeQuery(id+"F5.opRevolve","SWEPT_FACE",FACE,{"disambiguationData":[OSD([sQuery(id+"F4.wireOp",EDGE,"E147.bottom")])]})]});
            var Q203;
            Q203=makeQuery(id+"F5.boolean.opBoolean","INTERSECT",EDGE,{"derivedFrom":[makeQuery(id+"F1.opExtrude","SWEPT_FACE",FACE,{"disambiguationData":[OSD([sQuery(id+"F0.wireOp",EDGE,"E68")])]}),makeQuery(id+"F5.opRevolve","SWEPT_FACE",FACE,{"disambiguationData":[OSD([sQuery(id+"F4.wireOp",EDGE,"E147.top")])]})]});
            var Q204;
            Q204=makeQuery(id+"F5.boolean.opBoolean","INTERSECT",EDGE,{"derivedFrom":[makeQuery(id+"F1.opExtrude","SWEPT_FACE",FACE,{"disambiguationData":[OSD([sQuery(id+"F0.wireOp",EDGE,"E60")])]}),makeQuery(id+"F5.opRevolve","SWEPT_FACE",FACE,{"disambiguationData":[OSD([sQuery(id+"F4.wireOp",EDGE,"E147.top")])]})]});
            var Q205;
            Q205=makeQuery(id+"F5.boolean.opBoolean","INTERSECT",EDGE,{"derivedFrom":[makeQuery(id+"F1.opExtrude","SWEPT_FACE",FACE,{"disambiguationData":[OSD([sQuery(id+"F0.wireOp",EDGE,"E60")])]}),makeQuery(id+"F5.opRevolve","SWEPT_FACE",FACE,{"disambiguationData":[OSD([sQuery(id+"F4.wireOp",EDGE,"E147.bottom")])]})]});
            var Q206;
            Q206=makeQuery(id+"F5.boolean.opBoolean","INTERSECT",EDGE,{"derivedFrom":[makeQuery(id+"F1.opExtrude","SWEPT_FACE",FACE,{"disambiguationData":[OSD([sQuery(id+"F0.wireOp",EDGE,"E52")])]}),makeQuery(id+"F5.opRevolve","SWEPT_FACE",FACE,{"disambiguationData":[OSD([sQuery(id+"F4.wireOp",EDGE,"E147.bottom")])]})]});
            var Q207;
            Q207=makeQuery(id+"F5.boolean.opBoolean","INTERSECT",EDGE,{"derivedFrom":[makeQuery(id+"F1.opExtrude","SWEPT_FACE",FACE,{"disambiguationData":[OSD([sQuery(id+"F0.wireOp",EDGE,"E52")])]}),makeQuery(id+"F5.opRevolve","SWEPT_FACE",FACE,{"disambiguationData":[OSD([sQuery(id+"F4.wireOp",EDGE,"E147.top")])]})]});
            var Q208;
            Q208=makeQuery(id+"F5.boolean.opBoolean","INTERSECT",EDGE,{"derivedFrom":[makeQuery(id+"F1.opExtrude","SWEPT_FACE",FACE,{"disambiguationData":[OSD([sQuery(id+"F0.wireOp",EDGE,"E44")])]}),makeQuery(id+"F5.opRevolve","SWEPT_FACE",FACE,{"disambiguationData":[OSD([sQuery(id+"F4.wireOp",EDGE,"E147.bottom")])]})]});
            var Q209;
            Q209=makeQuery(id+"F5.boolean.opBoolean","INTERSECT",EDGE,{"derivedFrom":[makeQuery(id+"F1.opExtrude","SWEPT_FACE",FACE,{"disambiguationData":[OSD([sQuery(id+"F0.wireOp",EDGE,"E44")])]}),makeQuery(id+"F5.opRevolve","SWEPT_FACE",FACE,{"disambiguationData":[OSD([sQuery(id+"F4.wireOp",EDGE,"E147.top")])]})]});
            var Q210;
            Q210=makeQuery(id+"F5.boolean.opBoolean","INTERSECT",EDGE,{"derivedFrom":[makeQuery(id+"F1.opExtrude","SWEPT_FACE",FACE,{"disambiguationData":[OSD([sQuery(id+"F0.wireOp",EDGE,"E36")])]}),makeQuery(id+"F5.opRevolve","SWEPT_FACE",FACE,{"disambiguationData":[OSD([sQuery(id+"F4.wireOp",EDGE,"E147.top")])]})]});
            var Q211;
            Q211=makeQuery(id+"F5.boolean.opBoolean","INTERSECT",EDGE,{"derivedFrom":[makeQuery(id+"F1.opExtrude","SWEPT_FACE",FACE,{"disambiguationData":[OSD([sQuery(id+"F0.wireOp",EDGE,"E36")])]}),makeQuery(id+"F5.opRevolve","SWEPT_FACE",FACE,{"disambiguationData":[OSD([sQuery(id+"F4.wireOp",EDGE,"E147.bottom")])]})]});
            var Q212;
            Q212=makeQuery(id+"F5.boolean.opBoolean","INTERSECT",EDGE,{"derivedFrom":[makeQuery(id+"F1.opExtrude","SWEPT_FACE",FACE,{"disambiguationData":[OSD([sQuery(id+"F0.wireOp",EDGE,"E28")])]}),makeQuery(id+"F5.opRevolve","SWEPT_FACE",FACE,{"disambiguationData":[OSD([sQuery(id+"F4.wireOp",EDGE,"E147.bottom")])]})]});
            var Q213;
            Q213=makeQuery(id+"F5.boolean.opBoolean","INTERSECT",EDGE,{"derivedFrom":[makeQuery(id+"F1.opExtrude","SWEPT_FACE",FACE,{"disambiguationData":[OSD([sQuery(id+"F0.wireOp",EDGE,"E28")])]}),makeQuery(id+"F5.opRevolve","SWEPT_FACE",FACE,{"disambiguationData":[OSD([sQuery(id+"F4.wireOp",EDGE,"E147.top")])]})]});
            var Q214;
            Q214=makeQuery(id+"F5.boolean.opBoolean","INTERSECT",EDGE,{"derivedFrom":[makeQuery(id+"F1.opExtrude","SWEPT_FACE",FACE,{"disambiguationData":[OSD([sQuery(id+"F0.wireOp",EDGE,"E30")])]}),makeQuery(id+"F5.opRevolve","SWEPT_FACE",FACE,{"disambiguationData":[OSD([sQuery(id+"F4.wireOp",EDGE,"E147.bottom")])]})]});
            var Q215;
            Q215=makeQuery(id+"F5.boolean.opBoolean","INTERSECT",EDGE,{"derivedFrom":[makeQuery(id+"F1.opExtrude","SWEPT_FACE",FACE,{"disambiguationData":[OSD([sQuery(id+"F0.wireOp",EDGE,"E30")])]}),makeQuery(id+"F5.opRevolve","SWEPT_FACE",FACE,{"disambiguationData":[OSD([sQuery(id+"F4.wireOp",EDGE,"E147.top")])]})]});
            var Q216;
            Q216=makeQuery(id+"F5.boolean.opBoolean","INTERSECT",EDGE,{"derivedFrom":[makeQuery(id+"F1.opExtrude","SWEPT_FACE",FACE,{"disambiguationData":[OSD([sQuery(id+"F0.wireOp",EDGE,"E20")])]}),makeQuery(id+"F5.opRevolve","SWEPT_FACE",FACE,{"disambiguationData":[OSD([sQuery(id+"F4.wireOp",EDGE,"E147.bottom")])]})]});
            var Q217;
            Q217=makeQuery(id+"F5.boolean.opBoolean","INTERSECT",EDGE,{"derivedFrom":[makeQuery(id+"F1.opExtrude","SWEPT_FACE",FACE,{"disambiguationData":[OSD([sQuery(id+"F0.wireOp",EDGE,"E20")])]}),makeQuery(id+"F5.opRevolve","SWEPT_FACE",FACE,{"disambiguationData":[OSD([sQuery(id+"F4.wireOp",EDGE,"E147.top")])]})]});
            chamfer(context, id + "F6", {"entities" : qUnion([Q0, Q1, Q2, Q3, Q4, Q5, Q6, Q7, Q8, Q9, Q10, Q11, Q12, Q13, Q14, Q15, Q16, Q17, Q18, Q19, Q20, Q21, Q22, Q23, Q24, Q25, Q26, Q27, Q28, Q29, Q30, Q31, Q32, Q33, Q34, Q35, Q36, Q37, Q38, Q39, Q40, Q41, Q42, Q43, Q44, Q45, Q46, Q47, Q48, Q49, Q50, Q51, Q52, Q53, Q54, Q55, Q56, Q57, Q58, Q59, Q60, Q61, Q62, Q63, Q64, Q65, Q66, Q67, Q68, Q69, Q70, Q71, Q72, Q73, Q74, Q75, Q76, Q77, Q78, Q79, Q80, Q81, Q82, Q83, Q84, Q85, Q86, Q87, Q88, Q89, Q90, Q91, Q92, Q93, Q94, Q95, Q96, Q97, Q98, Q99, Q100, Q101, Q102, Q103, Q104, Q105, Q106, Q107, Q108, Q109, Q110, Q111, Q112, Q113, Q114, Q115, Q116, Q117, Q118, Q119, Q120, Q121, Q122, Q123, Q124, Q125, Q126, Q127, Q128, Q129, Q130, Q131, Q132, Q133, Q134, Q135, Q136, Q137, Q138, Q139, Q140, Q141, Q142, Q143, Q144, Q145, Q146, Q147, Q148, Q149, Q150, Q151, Q152, Q153, Q154, Q155, Q156, Q157, Q158, Q159, Q160, Q161, Q162, Q163, Q164, Q165, Q166, Q167, Q168, Q169, Q170, Q171, Q172, Q173, Q174, Q175, Q176, Q177, Q178, Q179, Q180, Q181, Q182, Q183, Q184, Q185, Q186, Q187, Q188, Q189, Q190, Q191, Q192, Q193, Q194, Q195, Q196, Q197, Q198, Q199, Q200, Q201, Q202, Q203, Q204, Q205, Q206, Q207, Q208, Q209, Q210, Q211, Q212, Q213, Q214, Q215, Q216, Q217]), "width" : 1 * mm, "tangentPropagation" : true});
        }
    });
